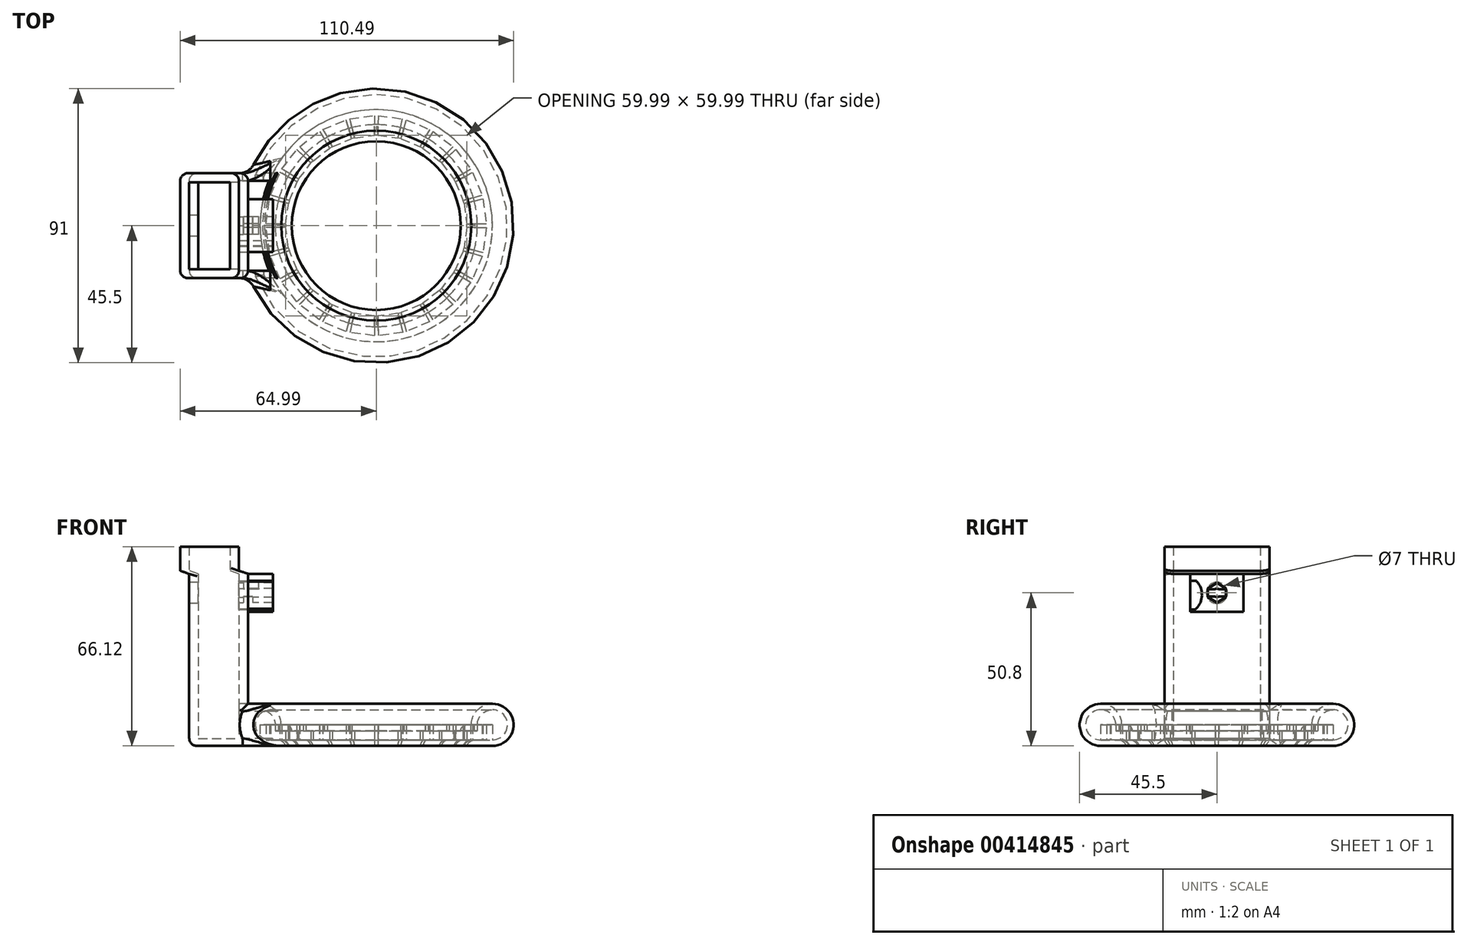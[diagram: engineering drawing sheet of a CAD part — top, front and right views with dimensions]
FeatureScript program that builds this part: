
annotation { "Feature Type Name" : "Feature", "Feature Type Description" : "" }
export const myFeature = defineFeature(function(context is Context, id is Id, definition is map)
    precondition{}
    {
        {
            var Q0;
            Q0=qCreatedBy(makeId("Right.planeOp"),FACE);
            cPlane(context, id + "F0", {"entities" : qUnion([Q0]), "cplaneType" : CPlaneType.OFFSET, "offset" : 42.5 * mm, "oppositeDirection" : true, "width" : 150 * mm, "height" : 150 * mm});
        }
        {
            var Q0;
            Q0=qCreatedBy(makeId("Front.planeOp"),FACE);
            cPlane(context, id + "F1", {"entities" : qUnion([Q0]), "cplaneType" : CPlaneType.OFFSET, "offset" : 17.41 * mm, "width" : 150 * mm, "height" : 150 * mm});
        }
        {
            var Q0;
            Q0=qCreatedBy(makeId("Front.planeOp"),FACE);
            cPlane(context, id + "F2", {"entities" : qUnion([Q0]), "cplaneType" : CPlaneType.OFFSET, "offset" : 17.41 * mm, "oppositeDirection" : true, "width" : 150 * mm, "height" : 150 * mm});
        }
        {
            var Q0;
            Q0=qCreatedBy(makeId("Top.planeOp"),FACE);
            cPlane(context, id + "F3", {"entities" : qUnion([Q0]), "cplaneType" : CPlaneType.OFFSET, "offset" : 7 * mm, "width" : 150 * mm, "height" : 150 * mm});
        }
        {
            var Q0;
            Q0=qCreatedBy(id+"F3.planeOp",FACE);
            cPlane(context, id + "F4", {"entities" : qUnion([Q0]), "cplaneType" : CPlaneType.OFFSET, "offset" : 6.95 * mm, "width" : 150 * mm, "height" : 150 * mm});
        }
        {
            var Q0;
            Q0=qCreatedBy(id+"F3.planeOp",FACE);
            cPlane(context, id + "F5", {"entities" : qUnion([Q0]), "cplaneType" : CPlaneType.OFFSET, "offset" : 50.12 * mm, "width" : 150 * mm, "height" : 150 * mm});
        }
        {
            var Q0;
            Q0=qCreatedBy(makeId("Right.planeOp"),FACE);
            cPlane(context, id + "F6", {"entities" : qUnion([Q0]), "cplaneType" : CPlaneType.OFFSET, "offset" : 62 * mm, "oppositeDirection" : true, "width" : 150 * mm, "height" : 150 * mm});
        }
        {
            var Q0;
            Q0=qCreatedBy(id+"F5.planeOp",FACE);
            cPlane(context, id + "F7", {"entities" : qUnion([Q0]), "cplaneType" : CPlaneType.OFFSET, "offset" : 1 * mm, "width" : 150 * mm, "height" : 150 * mm});
        }
        {
            var Q0;
            Q0=qCreatedBy(makeId("Top.planeOp"),FACE);
            var sketch = newSketch(context, id + "F8", { "sketchPlane" : qUnion([Q0])});
            skCircle(sketch, "E0", {"center": v(0, 0) * mm, "radius": 45 * mm});
            skCircle(sketch, "E1.0", {"center": v(0, 0) * mm, "radius": 38.5 * mm});
            skLineSegment(sketch, "E2", {"start": v(-136.41, 41.5) * mm, "end": v(-136.41, 35) * mm});
            skLineSegment(sketch, "E3", {"start": v(-128.72, 34) * mm, "end": v(-127.05, 40.28) * mm});
            skLineSegment(sketch, "E4", {"start": v(-118.16, 36.6) * mm, "end": v(-121.4, 30.99) * mm});
            skLineSegment(sketch, "E5", {"start": v(-115.15, 26.17) * mm, "end": v(-110.55, 30.76) * mm});
            skLineSegment(sketch, "E6", {"start": v(-110.44, 20.01) * mm, "end": v(-104.8, 23.26) * mm});
            skLineSegment(sketch, "E7", {"start": v(-107.45, 12.84) * mm, "end": v(-101.18, 14.54) * mm});
            skLineSegment(sketch, "E8", {"start": v(-106.41, 5.01) * mm, "end": v(-99.91, 5.01) * mm});
            skLineSegment(sketch, "E9.MirrorCS", {"start": v(-107.44, -2.81) * mm, "end": v(-101.17, -4.5) * mm});
            skLineSegment(sketch, "E10.MirrorCS", {"start": v(-110.42, -9.99) * mm, "end": v(-104.8, -13.24) * mm});
            skLineSegment(sketch, "E11.MirrorCS", {"start": v(-115.13, -16.15) * mm, "end": v(-110.52, -20.73) * mm});
            skLineSegment(sketch, "E12.MirrorCS", {"start": v(-118.13, -26.6) * mm, "end": v(-121.38, -20.97) * mm});
            skLineSegment(sketch, "E13.MirrorCS", {"start": v(-128.7, -24) * mm, "end": v(-127.02, -30.27) * mm});
            skLineSegment(sketch, "E14.MirrorCS", {"start": v(-144.1, 34) * mm, "end": v(-145.77, 40.28) * mm});
            skLineSegment(sketch, "E15.MirrorCS", {"start": v(-154.66, 36.6) * mm, "end": v(-151.41, 30.99) * mm});
            skLineSegment(sketch, "E16.MirrorCS", {"start": v(-157.67, 26.17) * mm, "end": v(-162.27, 30.76) * mm});
            skLineSegment(sketch, "E17.MirrorCS", {"start": v(-162.38, 20.01) * mm, "end": v(-168.01, 23.26) * mm});
            skLineSegment(sketch, "E18.MirrorCS", {"start": v(-165.37, 12.84) * mm, "end": v(-171.64, 14.54) * mm});
            skLineSegment(sketch, "E19.MirrorCS", {"start": v(-165.38, -2.81) * mm, "end": v(-171.65, -4.5) * mm});
            skLineSegment(sketch, "E20.MirrorCS", {"start": v(-162.4, -9.99) * mm, "end": v(-168.03, -13.24) * mm});
            skLineSegment(sketch, "E21.MirrorCS", {"start": v(-157.69, -16.15) * mm, "end": v(-162.3, -20.73) * mm});
            skLineSegment(sketch, "E22.MirrorCS", {"start": v(-154.69, -26.6) * mm, "end": v(-151.44, -20.97) * mm});
            skLineSegment(sketch, "E23.MirrorCS", {"start": v(-144.13, -24) * mm, "end": v(-145.8, -30.27) * mm});
            skLineSegment(sketch, "E24", {"start": v(-136.41, -25) * mm, "end": v(-136.41, -31.5) * mm});
            skLineSegment(sketch, "E25", {"start": v(-166.41, 5) * mm, "end": v(-172.91, 5) * mm});
            skCircle(sketch, "E26", {"center": v(-136.41, 5) * mm, "radius": 1.25 * mm, "construction": true});
            skLineSegment(sketch, "E27", {"start": v(0.64, 36.5) * mm, "end": v(0.52, 30) * mm});
            skLineSegment(sketch, "E28", {"start": v(8.2, 28.86) * mm, "end": v(9.97, 35.11) * mm});
            skLineSegment(sketch, "E29", {"start": v(18.8, 31.29) * mm, "end": v(15.46, 25.72) * mm});
            skLineSegment(sketch, "E30", {"start": v(21.62, 20.8) * mm, "end": v(26.3, 25.3) * mm});
            skLineSegment(sketch, "E31", {"start": v(26.23, 14.56) * mm, "end": v(31.92, 17.71) * mm});
            skLineSegment(sketch, "E32", {"start": v(29.1, 7.33) * mm, "end": v(35.4, 8.92) * mm});
            skLineSegment(sketch, "E33", {"start": v(30, -0.5) * mm, "end": v(36.5, -0.62) * mm});
            skLineSegment(sketch, "E34.MirrorCS", {"start": v(28.82, -8.32) * mm, "end": v(35.07, -10.12) * mm});
            skLineSegment(sketch, "E35.MirrorCS", {"start": v(25.72, -15.44) * mm, "end": v(31.3, -18.78) * mm});
            skLineSegment(sketch, "E36.MirrorCS", {"start": v(20.9, -21.52) * mm, "end": v(25.43, -26.18) * mm});
            skLineSegment(sketch, "E37.MirrorCS", {"start": v(17.73, -31.9) * mm, "end": v(14.57, -26.23) * mm});
            skLineSegment(sketch, "E38.MirrorCS", {"start": v(7.21, -29.12) * mm, "end": v(8.77, -35.43) * mm});
            skLineSegment(sketch, "E39.MirrorCS", {"start": v(-7.18, 29.13) * mm, "end": v(-8.74, 35.44) * mm});
            skLineSegment(sketch, "E40.MirrorCS", {"start": v(-17.7, 31.92) * mm, "end": v(-14.55, 26.25) * mm});
            skLineSegment(sketch, "E41.MirrorCS", {"start": v(-20.88, 21.54) * mm, "end": v(-25.4, 26.2) * mm});
            skLineSegment(sketch, "E42.MirrorCS", {"start": v(-25.7, 15.46) * mm, "end": v(-31.28, 18.81) * mm});
            skLineSegment(sketch, "E43.MirrorCS", {"start": v(-28.82, 8.34) * mm, "end": v(-35.06, 10.15) * mm});
            skLineSegment(sketch, "E44.MirrorCS", {"start": v(-29.1, -7.3) * mm, "end": v(-35.4, -8.89) * mm});
            skLineSegment(sketch, "E45.MirrorCS", {"start": v(-26.25, -14.53) * mm, "end": v(-31.93, -17.68) * mm});
            skLineSegment(sketch, "E46.MirrorCS", {"start": v(-21.64, -20.77) * mm, "end": v(-26.33, -25.28) * mm});
            skLineSegment(sketch, "E47.MirrorCS", {"start": v(-18.83, -31.27) * mm, "end": v(-15.48, -25.7) * mm});
            skLineSegment(sketch, "E48.MirrorCS", {"start": v(-8.22, -28.85) * mm, "end": v(-10, -35.1) * mm});
            skLineSegment(sketch, "E49", {"start": v(-0.52, -30) * mm, "end": v(-0.64, -36.5) * mm});
            skLineSegment(sketch, "E50", {"start": v(-30, 0.52) * mm, "end": v(-36.5, 0.64) * mm});
            skLineSegment(sketch, "E51", {"start": v(-0.64, 36.5) * mm, "end": v(-0.52, 30) * mm});
            skLineSegment(sketch, "E52", {"start": v(7.18, 29.13) * mm, "end": v(8.74, 35.44) * mm});
            skLineSegment(sketch, "E53", {"start": v(17.7, 31.92) * mm, "end": v(14.55, 26.25) * mm});
            skLineSegment(sketch, "E54", {"start": v(20.88, 21.54) * mm, "end": v(25.4, 26.2) * mm});
            skLineSegment(sketch, "E55", {"start": v(25.7, 15.46) * mm, "end": v(31.28, 18.81) * mm});
            skLineSegment(sketch, "E56", {"start": v(28.82, 8.34) * mm, "end": v(35.06, 10.15) * mm});
            skLineSegment(sketch, "E57", {"start": v(30, 0.54) * mm, "end": v(36.5, 0.65) * mm});
            skLineSegment(sketch, "E58.MirrorCS", {"start": v(29.1, -7.3) * mm, "end": v(35.4, -8.89) * mm});
            skLineSegment(sketch, "E59.MirrorCS", {"start": v(26.25, -14.53) * mm, "end": v(31.93, -17.68) * mm});
            skLineSegment(sketch, "E60.MirrorCS", {"start": v(21.64, -20.77) * mm, "end": v(26.33, -25.28) * mm});
            skLineSegment(sketch, "E61.MirrorCS", {"start": v(18.83, -31.27) * mm, "end": v(15.48, -25.7) * mm});
            skLineSegment(sketch, "E62.MirrorCS", {"start": v(8.22, -28.85) * mm, "end": v(10, -35.1) * mm});
            skLineSegment(sketch, "E63.MirrorCS", {"start": v(-8.2, 28.86) * mm, "end": v(-9.97, 35.11) * mm});
            skLineSegment(sketch, "E64.MirrorCS", {"start": v(-18.8, 31.29) * mm, "end": v(-15.46, 25.72) * mm});
            skLineSegment(sketch, "E65.MirrorCS", {"start": v(-21.62, 20.8) * mm, "end": v(-26.3, 25.3) * mm});
            skLineSegment(sketch, "E66.MirrorCS", {"start": v(-26.23, 14.56) * mm, "end": v(-31.92, 17.71) * mm});
            skLineSegment(sketch, "E67.MirrorCS", {"start": v(-29.1, 7.33) * mm, "end": v(-35.4, 8.92) * mm});
            skLineSegment(sketch, "E68.MirrorCS", {"start": v(-28.82, -8.32) * mm, "end": v(-35.07, -10.12) * mm});
            skLineSegment(sketch, "E69.MirrorCS", {"start": v(-25.72, -15.44) * mm, "end": v(-31.3, -18.78) * mm});
            skLineSegment(sketch, "E70.MirrorCS", {"start": v(-20.9, -21.52) * mm, "end": v(-25.43, -26.18) * mm});
            skLineSegment(sketch, "E71.MirrorCS", {"start": v(-17.73, -31.9) * mm, "end": v(-14.57, -26.23) * mm});
            skLineSegment(sketch, "E72.MirrorCS", {"start": v(-7.21, -29.12) * mm, "end": v(-8.77, -35.43) * mm});
            skLineSegment(sketch, "E73", {"start": v(0.52, -30) * mm, "end": v(0.64, -36.5) * mm});
            skLineSegment(sketch, "E74", {"start": v(-30, -0.52) * mm, "end": v(-36.5, -0.64) * mm});
            skCircle(sketch, "E75", {"center": v(0, 0) * mm, "radius": 1.25 * mm, "construction": true});
            skLineSegment(sketch, "E76", {"start": v(-29.1, 7.33) * mm, "end": v(-28.82, 8.34) * mm});
            skLineSegment(sketch, "E77", {"start": v(-28.82, 8.34) * mm, "end": v(-26.23, 14.56) * mm});
            skLineSegment(sketch, "E78", {"start": v(-26.23, 14.56) * mm, "end": v(-25.7, 15.46) * mm});
            skLineSegment(sketch, "E79", {"start": v(-25.7, 15.46) * mm, "end": v(-21.62, 20.8) * mm});
            skLineSegment(sketch, "E80", {"start": v(-21.62, 20.8) * mm, "end": v(-20.88, 21.54) * mm});
            skLineSegment(sketch, "E81", {"start": v(-20.88, 21.54) * mm, "end": v(-15.46, 25.72) * mm});
            skLineSegment(sketch, "E82", {"start": v(-15.46, 25.72) * mm, "end": v(-14.55, 26.25) * mm});
            skLineSegment(sketch, "E83", {"start": v(-14.55, 26.25) * mm, "end": v(-8.2, 28.86) * mm});
            skLineSegment(sketch, "E84", {"start": v(-8.2, 28.86) * mm, "end": v(-7.18, 29.13) * mm});
            skLineSegment(sketch, "E85", {"start": v(-7.18, 29.13) * mm, "end": v(-0.52, 30) * mm});
            skLineSegment(sketch, "E86", {"start": v(-0.52, 30) * mm, "end": v(0.52, 30) * mm});
            skLineSegment(sketch, "E87", {"start": v(0.52, 30) * mm, "end": v(7.18, 29.13) * mm});
            skLineSegment(sketch, "E88", {"start": v(7.18, 29.13) * mm, "end": v(8.2, 28.86) * mm});
            skLineSegment(sketch, "E89", {"start": v(8.2, 28.86) * mm, "end": v(14.55, 26.25) * mm});
            skLineSegment(sketch, "E90", {"start": v(14.55, 26.25) * mm, "end": v(15.46, 25.72) * mm});
            skLineSegment(sketch, "E91", {"start": v(15.46, 25.72) * mm, "end": v(20.88, 21.54) * mm});
            skLineSegment(sketch, "E92", {"start": v(20.88, 21.54) * mm, "end": v(21.62, 20.8) * mm});
            skLineSegment(sketch, "E93", {"start": v(21.62, 20.8) * mm, "end": v(25.7, 15.46) * mm});
            skLineSegment(sketch, "E94", {"start": v(25.7, 15.46) * mm, "end": v(26.23, 14.56) * mm});
            skLineSegment(sketch, "E95", {"start": v(26.23, 14.56) * mm, "end": v(28.82, 8.34) * mm});
            skLineSegment(sketch, "E96", {"start": v(28.82, 8.34) * mm, "end": v(29.1, 7.33) * mm});
            skLineSegment(sketch, "E97", {"start": v(29.1, 7.33) * mm, "end": v(30, 0.54) * mm});
            skLineSegment(sketch, "E98", {"start": v(30, 0.54) * mm, "end": v(30, -0.5) * mm});
            skLineSegment(sketch, "E99", {"start": v(30, -0.5) * mm, "end": v(29.1, -7.3) * mm});
            skLineSegment(sketch, "E100", {"start": v(29.1, -7.3) * mm, "end": v(28.82, -8.32) * mm});
            skLineSegment(sketch, "E101", {"start": v(28.82, -8.32) * mm, "end": v(26.25, -14.53) * mm});
            skLineSegment(sketch, "E102", {"start": v(26.25, -14.53) * mm, "end": v(25.72, -15.44) * mm});
            skLineSegment(sketch, "E103", {"start": v(25.72, -15.44) * mm, "end": v(21.64, -20.77) * mm});
            skLineSegment(sketch, "E104", {"start": v(21.64, -20.77) * mm, "end": v(20.9, -21.52) * mm});
            skLineSegment(sketch, "E105", {"start": v(20.9, -21.52) * mm, "end": v(15.48, -25.7) * mm});
            skLineSegment(sketch, "E106", {"start": v(15.48, -25.7) * mm, "end": v(14.57, -26.23) * mm});
            skLineSegment(sketch, "E107", {"start": v(14.57, -26.23) * mm, "end": v(8.22, -28.85) * mm});
            skLineSegment(sketch, "E108", {"start": v(8.22, -28.85) * mm, "end": v(7.21, -29.12) * mm});
            skLineSegment(sketch, "E109", {"start": v(7.21, -29.12) * mm, "end": v(0.52, -30) * mm});
            skLineSegment(sketch, "E110", {"start": v(0.52, -30) * mm, "end": v(-0.52, -30) * mm});
            skLineSegment(sketch, "E111", {"start": v(-0.52, -30) * mm, "end": v(-7.21, -29.12) * mm});
            skLineSegment(sketch, "E112", {"start": v(-7.21, -29.12) * mm, "end": v(-8.22, -28.85) * mm});
            skLineSegment(sketch, "E113", {"start": v(-8.22, -28.85) * mm, "end": v(-14.57, -26.23) * mm});
            skLineSegment(sketch, "E114", {"start": v(-14.57, -26.23) * mm, "end": v(-15.48, -25.7) * mm});
            skLineSegment(sketch, "E115", {"start": v(-15.48, -25.7) * mm, "end": v(-20.9, -21.52) * mm});
            skLineSegment(sketch, "E116", {"start": v(-20.9, -21.52) * mm, "end": v(-21.64, -20.77) * mm});
            skLineSegment(sketch, "E117", {"start": v(-21.64, -20.77) * mm, "end": v(-25.72, -15.44) * mm});
            skLineSegment(sketch, "E118", {"start": v(-25.72, -15.44) * mm, "end": v(-26.25, -14.53) * mm});
            skLineSegment(sketch, "E119", {"start": v(-28.82, -8.32) * mm, "end": v(-29.1, -7.3) * mm});
            skLineSegment(sketch, "E120", {"start": v(-26.25, -14.53) * mm, "end": v(-28.82, -8.32) * mm});
            skLineSegment(sketch, "E121", {"start": v(-29.1, -7.3) * mm, "end": v(-30, -0.52) * mm});
            skLineSegment(sketch, "E122", {"start": v(-30, -0.52) * mm, "end": v(-30, 0.52) * mm});
            skLineSegment(sketch, "E123", {"start": v(-30, 0.52) * mm, "end": v(-29.1, 7.33) * mm});
            skLineSegment(sketch, "E124", {"start": v(-36.5, 0.64) * mm, "end": v(-35.4, 8.92) * mm});
            skLineSegment(sketch, "E125", {"start": v(-35.06, 10.15) * mm, "end": v(-31.92, 17.71) * mm});
            skLineSegment(sketch, "E126", {"start": v(-31.28, 18.81) * mm, "end": v(-26.3, 25.3) * mm});
            skLineSegment(sketch, "E127", {"start": v(-25.4, 26.2) * mm, "end": v(-18.8, 31.29) * mm});
            skLineSegment(sketch, "E128", {"start": v(-17.7, 31.92) * mm, "end": v(-9.97, 35.11) * mm});
            skLineSegment(sketch, "E129", {"start": v(-8.74, 35.44) * mm, "end": v(-0.64, 36.5) * mm});
            skLineSegment(sketch, "E130", {"start": v(0.64, 36.5) * mm, "end": v(8.74, 35.44) * mm});
            skLineSegment(sketch, "E131", {"start": v(9.97, 35.11) * mm, "end": v(17.7, 31.92) * mm});
            skLineSegment(sketch, "E132", {"start": v(18.8, 31.29) * mm, "end": v(25.4, 26.2) * mm});
            skLineSegment(sketch, "E133", {"start": v(26.3, 25.3) * mm, "end": v(31.28, 18.81) * mm});
            skLineSegment(sketch, "E134", {"start": v(31.92, 17.71) * mm, "end": v(35.06, 10.15) * mm});
            skLineSegment(sketch, "E135", {"start": v(35.4, 8.92) * mm, "end": v(36.5, 0.65) * mm});
            skLineSegment(sketch, "E136", {"start": v(36.5, -0.62) * mm, "end": v(35.4, -8.89) * mm});
            skLineSegment(sketch, "E137", {"start": v(35.07, -10.12) * mm, "end": v(31.93, -17.68) * mm});
            skLineSegment(sketch, "E138", {"start": v(31.3, -18.78) * mm, "end": v(26.33, -25.28) * mm});
            skLineSegment(sketch, "E139", {"start": v(25.43, -26.18) * mm, "end": v(18.83, -31.27) * mm});
            skLineSegment(sketch, "E140", {"start": v(17.73, -31.9) * mm, "end": v(10, -35.1) * mm});
            skLineSegment(sketch, "E141", {"start": v(8.77, -35.43) * mm, "end": v(0.64, -36.5) * mm});
            skLineSegment(sketch, "E142", {"start": v(-0.64, -36.5) * mm, "end": v(-8.77, -35.43) * mm});
            skLineSegment(sketch, "E143", {"start": v(-10, -35.1) * mm, "end": v(-17.73, -31.9) * mm});
            skLineSegment(sketch, "E144", {"start": v(-18.83, -31.27) * mm, "end": v(-25.43, -26.18) * mm});
            skLineSegment(sketch, "E145", {"start": v(-26.33, -25.28) * mm, "end": v(-31.3, -18.78) * mm});
            skLineSegment(sketch, "E146", {"start": v(-31.93, -17.68) * mm, "end": v(-35.07, -10.12) * mm});
            skLineSegment(sketch, "E147", {"start": v(-35.4, -8.89) * mm, "end": v(-36.5, -0.64) * mm});
            skSolve(sketch);
        }
        {
            var Q0;
            Q0=qCreatedBy(makeId("Front.planeOp"),FACE);
            var sketch = newSketch(context, id + "F9", { "sketchPlane" : qUnion([Q0])});
            skLineSegment(sketch, "E148.bottom", {"start": v(38.5, 7) * mm, "end": v(-38.5, 7) * mm, "construction": true});
            skLineSegment(sketch, "E148.top", {"start": v(38.5, -7) * mm, "end": v(-38.5, -7) * mm, "construction": true});
            skLineSegment(sketch, "E148.left", {"start": v(38.5, 7) * mm, "end": v(38.5, -7) * mm, "construction": true});
            skLineSegment(sketch, "E148.right", {"start": v(-38.5, 7) * mm, "end": v(-38.5, -7) * mm, "construction": true});
            skPoint(sketch, "E148.middle", {"position": v(0, 0) * mm});
            skLineSegment(sketch, "E149", {"start": v(-38.5, 0) * mm, "end": v(38.5, 0) * mm, "construction": true});
            skArc(sketch, "E150", {"start": v(38.5, 0) * mm, "mid": v(43.45, 11.95) * mm, "end": v(31.5, 7) * mm});
            skArc(sketch, "E151", {"start": v(38.5, 2) * mm, "mid": v(42.04, 10.54) * mm, "end": v(33.5, 7) * mm});
            skLineSegment(sketch, "E152", {"start": v(38.5, 2) * mm, "end": v(38.5, 0) * mm});
            skLineSegment(sketch, "E153", {"start": v(38.5, 2) * mm, "end": v(31.5, 2) * mm, "construction": true});
            skLineSegment(sketch, "E154", {"start": v(31.5, 2) * mm, "end": v(31.5, 0) * mm, "construction": true});
            skLineSegment(sketch, "E155.0", {"start": v(38.5, 5) * mm, "end": v(-38.5, 5) * mm, "construction": true});
            skLineSegment(sketch, "E156", {"start": v(30, 0) * mm, "end": v(30, 7) * mm, "construction": true});
            skLineSegment(sketch, "E157", {"start": v(31.5, 7) * mm, "end": v(30, 7) * mm});
            skLineSegment(sketch, "E158", {"start": v(30, 7) * mm, "end": v(30, 5) * mm});
            skLineSegment(sketch, "E159", {"start": v(30, 5) * mm, "end": v(33.5, 5) * mm});
            skLineSegment(sketch, "E160", {"start": v(33.5, 5) * mm, "end": v(33.5, 7) * mm});
            skLineSegment(sketch, "E161", {"start": v(0, -7) * mm, "end": v(0, 7) * mm, "construction": true});
            skLineSegment(sketch, "E162", {"start": v(38.5, 7) * mm, "end": v(38.5, 14) * mm, "construction": true});
            skLineSegment(sketch, "E163", {"start": v(38.5, 7) * mm, "end": v(45.5, 7) * mm, "construction": true});
            skLineSegment(sketch, "E164", {"start": v(38.5, 12) * mm, "end": v(38.5, 14) * mm});
            skLineSegment(sketch, "E165", {"start": v(43.5, 7) * mm, "end": v(45.5, 7) * mm});
            skLineSegment(sketch, "E166.MirrorCS", {"start": v(-38.5, 2) * mm, "end": v(-38.5, 0) * mm});
            skLineSegment(sketch, "E167.MirrorCS", {"start": v(-30, 7) * mm, "end": v(-30, 5) * mm});
            skLineSegment(sketch, "E168.MirrorCS", {"start": v(-31.5, 7) * mm, "end": v(-30, 7) * mm});
            skLineSegment(sketch, "E169.MirrorCS", {"start": v(-33.5, 5) * mm, "end": v(-33.5, 7) * mm});
            skLineSegment(sketch, "E170.MirrorCS", {"start": v(-43.5, 7) * mm, "end": v(-45.5, 7) * mm});
            skLineSegment(sketch, "E171.MirrorCS", {"start": v(-30, 5) * mm, "end": v(-33.5, 5) * mm});
            skLineSegment(sketch, "E172.MirrorCS", {"start": v(-31.5, 2) * mm, "end": v(-31.5, 0) * mm, "construction": true});
            skLineSegment(sketch, "E173.MirrorCS", {"start": v(-38.5, 12) * mm, "end": v(-38.5, 14) * mm});
            skLineSegment(sketch, "E174.MirrorCS", {"start": v(-38.5, 7) * mm, "end": v(-45.5, 7) * mm, "construction": true});
            skLineSegment(sketch, "E175.MirrorCS", {"start": v(-38.5, 2) * mm, "end": v(-31.5, 2) * mm, "construction": true});
            skLineSegment(sketch, "E176.MirrorCS", {"start": v(-38.5, 7) * mm, "end": v(-38.5, 14) * mm, "construction": true});
            skArc(sketch, "E177.MirrorCS", {"start": v(-38.5, 0) * mm, "mid": v(-43.45, 11.95) * mm, "end": v(-31.5, 7) * mm});
            skArc(sketch, "E178.MirrorCS", {"start": v(-38.5, 2) * mm, "mid": v(-42.04, 10.54) * mm, "end": v(-33.5, 7) * mm});
            skLineSegment(sketch, "E179.MirrorCS", {"start": v(-38.5, 5) * mm, "end": v(38.5, 5) * mm, "construction": true});
            skLineSegment(sketch, "E180.MirrorCS", {"start": v(-30, 0) * mm, "end": v(-30, 7) * mm, "construction": true});
            skLineSegment(sketch, "E181.MirrorCS", {"start": v(-38.5, 7) * mm, "end": v(38.5, 7) * mm, "construction": true});
            skArc(sketch, "E182", {"start": v(30, 7) * mm, "mid": v(28.58, 6.41) * mm, "end": v(28, 5) * mm});
            skLineSegment(sketch, "E183", {"start": v(28, 5) * mm, "end": v(30, 5) * mm});
            skArc(sketch, "E184.MirrorCS", {"start": v(-30, 7) * mm, "mid": v(-28.58, 6.41) * mm, "end": v(-28, 5) * mm});
            skLineSegment(sketch, "E185", {"start": v(-30, 5) * mm, "end": v(-28, 5) * mm});
            skSolve(sketch);
        }
        {
            var Q0;
            Q0=qCreatedBy(id+"F0.planeOp",FACE);
            var sketch = newSketch(context, id + "F10", { "sketchPlane" : qUnion([Q0])});
            skLineSegment(sketch, "E186.bottom", {"start": v(45.5, 14) * mm, "end": v(-45.5, 14) * mm, "construction": true});
            skLineSegment(sketch, "E186.top", {"start": v(45.5, -14) * mm, "end": v(-45.5, -14) * mm, "construction": true});
            skLineSegment(sketch, "E186.left", {"start": v(45.5, 14) * mm, "end": v(45.5, -14) * mm, "construction": true});
            skLineSegment(sketch, "E186.right", {"start": v(-45.5, 14) * mm, "end": v(-45.5, -14) * mm, "construction": true});
            skPoint(sketch, "E186.middle", {"position": v(0, 0) * mm});
            skLineSegment(sketch, "E187", {"start": v(-45.5, 0) * mm, "end": v(45.5, 0) * mm, "construction": true});
            skLineSegment(sketch, "E188", {"start": v(0, 14) * mm, "end": v(0, -14) * mm, "construction": true});
            skLineSegment(sketch, "E189.0", {"start": v(-17.41, 14) * mm, "end": v(-17.41, -14) * mm, "construction": true});
            skLineSegment(sketch, "E190.MirrorCS", {"start": v(17.41, 14) * mm, "end": v(17.41, -14) * mm, "construction": true});
            skLineSegment(sketch, "E191.0", {"start": v(45.5, 7) * mm, "end": v(-45.5, 7) * mm, "construction": true});
            skLineSegment(sketch, "E192", {"start": v(-17.41, 14) * mm, "end": v(-17.41, 7) * mm});
            skLineSegment(sketch, "E193", {"start": v(-17.41, 7) * mm, "end": v(17.41, 7) * mm});
            skLineSegment(sketch, "E194", {"start": v(17.41, 7) * mm, "end": v(17.41, 14) * mm});
            skLineSegment(sketch, "E195", {"start": v(17.41, 14) * mm, "end": v(-17.41, 14) * mm});
            skLineSegment(sketch, "E196.0", {"start": v(45.5, 12) * mm, "end": v(-45.5, 12) * mm, "construction": true});
            skLineSegment(sketch, "E197.0", {"start": v(-14.73, 14) * mm, "end": v(-14.73, -14) * mm, "construction": true});
            skLineSegment(sketch, "E198.MirrorCS", {"start": v(14.73, 14) * mm, "end": v(14.73, -14) * mm, "construction": true});
            skLineSegment(sketch, "E199", {"start": v(-14.73, 7) * mm, "end": v(-14.73, 14) * mm});
            skLineSegment(sketch, "E200", {"start": v(14.73, 7) * mm, "end": v(14.73, 14) * mm});
            skLineSegment(sketch, "E201", {"start": v(17.41, 12) * mm, "end": v(-17.41, 12) * mm});
            skPoint(sketch, "E201.startSnap0", {"position": v(17.41, 10.5) * mm});
            skArc(sketch, "E202.0", {"start": v(6.63, 54.56) * mm, "mid": v(4.95, 49.97) * mm, "end": v(6.87, 45.48) * mm});
            skArc(sketch, "E203.MirrorCS", {"start": v(-6.63, 54.56) * mm, "mid": v(-4.95, 49.97) * mm, "end": v(-6.87, 45.48) * mm});
            skLineSegment(sketch, "E204", {"start": v(-6.63, 54.73) * mm, "end": v(6.63, 54.73) * mm});
            skLineSegment(sketch, "E205.1", {"start": v(-2.98, 46.95) * mm, "end": v(2.98, 46.95) * mm});
            skLineSegment(sketch, "E206", {"start": v(-8.8, 44.55) * mm, "end": v(-8.8, 57.13) * mm});
            skLineSegment(sketch, "E207.MirrorCS", {"start": v(8.8, 44.55) * mm, "end": v(8.8, 57.13) * mm});
            skLineSegment(sketch, "E208", {"start": v(-8.8, 57.13) * mm, "end": v(8.8, 57.13) * mm});
            skLineSegment(sketch, "E209", {"start": v(-6.63, 54.73) * mm, "end": v(-8.8, 54.73) * mm});
            skLineSegment(sketch, "E210", {"start": v(6.63, 54.73) * mm, "end": v(8.8, 54.73) * mm});
            skLineSegment(sketch, "E211", {"start": v(-2.98, 46.95) * mm, "end": v(-6.87, 45.27) * mm});
            skLineSegment(sketch, "E212", {"start": v(-6.87, 45.48) * mm, "end": v(-6.87, 45.27) * mm});
            skLineSegment(sketch, "E213.MirrorCS", {"start": v(2.98, 46.95) * mm, "end": v(6.87, 45.27) * mm});
            skLineSegment(sketch, "E214.MirrorCS", {"start": v(6.87, 45.48) * mm, "end": v(6.87, 45.27) * mm});
            skLineSegment(sketch, "E215", {"start": v(-8.8, 44.55) * mm, "end": v(8.8, 44.55) * mm});
            skLineSegment(sketch, "E216", {"start": v(6.87, 45.27) * mm, "end": v(8.8, 45.27) * mm});
            skLineSegment(sketch, "E217", {"start": v(-6.87, 45.27) * mm, "end": v(-8.8, 45.27) * mm});
            skCircle(sketch, "E218", {"center": v(0, 0) * mm, "radius": 1.5 * mm, "construction": true});
            skCircle(sketch, "E219", {"center": v(0, 50.8) * mm, "radius": 1.39 * mm});
            skLineSegment(sketch, "E220", {"start": v(6.63, 54.56) * mm, "end": v(6.63, 54.73) * mm});
            skLineSegment(sketch, "E221", {"start": v(-6.63, 54.56) * mm, "end": v(-6.63, 54.73) * mm});
            skLineSegment(sketch, "E222.1", {"start": v(0, 47.5) * mm, "end": v(2.95, 49.36) * mm});
            skLineSegment(sketch, "E222.2", {"start": v(-2.95, 49.36) * mm, "end": v(0, 47.5) * mm});
            skLineSegment(sketch, "E223.MirrorCS", {"start": v(0, 54.1) * mm, "end": v(2.95, 52.25) * mm});
            skLineSegment(sketch, "E224.MirrorCS", {"start": v(-2.95, 52.25) * mm, "end": v(0, 54.1) * mm});
            skLineSegment(sketch, "E225", {"start": v(2.95, 52.25) * mm, "end": v(2.95, 49.36) * mm});
            skLineSegment(sketch, "E226", {"start": v(-2.95, 52.25) * mm, "end": v(-2.95, 49.36) * mm});
            skCircle(sketch, "E227", {"center": v(0, 50.8) * mm, "radius": 1.25 * mm, "construction": true});
            skLineSegment(sketch, "E228", {"start": v(-2.95, 49.55) * mm, "end": v(2.95, 49.55) * mm});
            skLineSegment(sketch, "E229", {"start": v(-2.95, 52.05) * mm, "end": v(2.95, 52.05) * mm});
            skLineSegment(sketch, "E230", {"start": v(14.73, 14) * mm, "end": v(14.73, 52.5) * mm});
            skLineSegment(sketch, "E231", {"start": v(0, 55.8) * mm, "end": v(0, 14) * mm, "construction": true});
            skLineSegment(sketch, "E232.MirrorCS", {"start": v(-14.73, 14) * mm, "end": v(-14.73, 52.5) * mm});
            skLineSegment(sketch, "E233", {"start": v(17.41, 14) * mm, "end": v(17.41, 52.5) * mm});
            skLineSegment(sketch, "E234", {"start": v(-17.41, 14) * mm, "end": v(-17.41, 52.5) * mm});
            skLineSegment(sketch, "E235", {"start": v(-8.8, 57.13) * mm, "end": v(-17.41, 57.13) * mm});
            skLineSegment(sketch, "E236", {"start": v(8.8, 57.13) * mm, "end": v(17.41, 57.13) * mm});
            skLineSegment(sketch, "E237", {"start": v(17.41, 47.5) * mm, "end": v(17.41, 57.13) * mm});
            skLineSegment(sketch, "E238", {"start": v(14.73, 47.5) * mm, "end": v(14.73, 57.13) * mm});
            skLineSegment(sketch, "E239", {"start": v(-14.73, 47.5) * mm, "end": v(-14.73, 57.13) * mm});
            skLineSegment(sketch, "E240", {"start": v(-17.41, 47.5) * mm, "end": v(-17.41, 57.13) * mm});
            skSolve(sketch);
        }
        {
            var Q0;
            Q0=qCreatedBy(id+"F1.planeOp",FACE);
            var sketch = newSketch(context, id + "F11", { "sketchPlane" : qUnion([Q0])});
            skLineSegment(sketch, "E241.bottom", {"start": v(45.5, 14) * mm, "end": v(-45.5, 14) * mm, "construction": true});
            skLineSegment(sketch, "E241.top", {"start": v(45.5, -14) * mm, "end": v(-45.5, -14) * mm, "construction": true});
            skLineSegment(sketch, "E241.left", {"start": v(45.5, 14) * mm, "end": v(45.5, -14) * mm, "construction": true});
            skLineSegment(sketch, "E241.right", {"start": v(-45.5, 14) * mm, "end": v(-45.5, -14) * mm, "construction": true});
            skPoint(sketch, "E241.middle", {"position": v(0, 0) * mm});
            skLineSegment(sketch, "E242", {"start": v(-45.5, 0) * mm, "end": v(45.5, 0) * mm, "construction": true});
            skLineSegment(sketch, "E243", {"start": v(0, 14) * mm, "end": v(0, -14) * mm, "construction": true});
            skLineSegment(sketch, "E244.0", {"start": v(-17.41, 14) * mm, "end": v(-17.41, -14) * mm, "construction": true});
            skLineSegment(sketch, "E245.MirrorCS", {"start": v(17.41, 14) * mm, "end": v(17.41, -14) * mm, "construction": true});
            skLineSegment(sketch, "E246.0", {"start": v(45.5, 7) * mm, "end": v(-45.5, 7) * mm, "construction": true});
            skLineSegment(sketch, "E247", {"start": v(-17.41, 14) * mm, "end": v(-17.41, 7) * mm});
            skLineSegment(sketch, "E248", {"start": v(-17.41, 7) * mm, "end": v(17.41, 7) * mm});
            skLineSegment(sketch, "E249", {"start": v(17.41, 7) * mm, "end": v(17.41, 14) * mm});
            skLineSegment(sketch, "E250", {"start": v(17.41, 14) * mm, "end": v(-17.41, 14) * mm});
            skLineSegment(sketch, "E251.0", {"start": v(45.5, 12) * mm, "end": v(-45.5, 12) * mm, "construction": true});
            skLineSegment(sketch, "E252.0", {"start": v(-14.73, 14) * mm, "end": v(-14.73, -14) * mm, "construction": true});
            skLineSegment(sketch, "E253.MirrorCS", {"start": v(14.73, 14) * mm, "end": v(14.73, -14) * mm, "construction": true});
            skLineSegment(sketch, "E254", {"start": v(-14.73, 7) * mm, "end": v(-14.73, 14) * mm});
            skLineSegment(sketch, "E255", {"start": v(14.73, 7) * mm, "end": v(14.73, 14) * mm});
            skLineSegment(sketch, "E256", {"start": v(17.41, 12) * mm, "end": v(-17.41, 12) * mm});
            skPoint(sketch, "E256.startSnap0", {"position": v(17.41, 10.5) * mm});
            skLineSegment(sketch, "E257", {"start": v(45.5, 14) * mm, "end": v(45.5, 7) * mm});
            skCircle(sketch, "E258", {"center": v(-35.07, 7) * mm, "radius": 7 * mm, "construction": true});
            skArc(sketch, "E259", {"start": v(-35.07, 12) * mm, "mid": v(-40.07, 7) * mm, "end": v(-35.07, 2) * mm});
            skLineSegment(sketch, "E260", {"start": v(-35.07, 12) * mm, "end": v(-35.07, 14) * mm});
            skLineSegment(sketch, "E261", {"start": v(-35.07, 14) * mm, "end": v(-45.5, 14) * mm});
            skLineSegment(sketch, "E262", {"start": v(-45.5, 14) * mm, "end": v(-45.5, 0) * mm});
            skLineSegment(sketch, "E263", {"start": v(-45.5, 0) * mm, "end": v(-35.07, 0) * mm});
            skLineSegment(sketch, "E264", {"start": v(-35.07, 0) * mm, "end": v(-35.07, 2) * mm});
            skLineSegment(sketch, "E265.MirrorCS", {"start": v(45.5, 2) * mm, "end": v(-45.5, 2) * mm, "construction": true});
            skCircle(sketch, "E266", {"center": v(0, 7) * mm, "radius": 1.25 * mm, "construction": true});
            skSolve(sketch);
        }
        {
            var Q0;
            Q0=qCreatedBy(id+"F2.planeOp",FACE);
            var sketch = newSketch(context, id + "F12", { "sketchPlane" : qUnion([Q0])});
            skLineSegment(sketch, "E267.bottom", {"start": v(45.5, 14) * mm, "end": v(-45.5, 14) * mm, "construction": true});
            skLineSegment(sketch, "E267.top", {"start": v(45.5, -14) * mm, "end": v(-45.5, -14) * mm, "construction": true});
            skLineSegment(sketch, "E267.left", {"start": v(45.5, 14) * mm, "end": v(45.5, -14) * mm, "construction": true});
            skLineSegment(sketch, "E267.right", {"start": v(-45.5, 14) * mm, "end": v(-45.5, -14) * mm, "construction": true});
            skPoint(sketch, "E267.middle", {"position": v(0, 0) * mm});
            skLineSegment(sketch, "E268", {"start": v(-45.5, 0) * mm, "end": v(45.5, 0) * mm, "construction": true});
            skLineSegment(sketch, "E269", {"start": v(0, 14) * mm, "end": v(0, -14) * mm, "construction": true});
            skLineSegment(sketch, "E270.0", {"start": v(-17.41, 14) * mm, "end": v(-17.41, -14) * mm, "construction": true});
            skLineSegment(sketch, "E271.MirrorCS", {"start": v(17.41, 14) * mm, "end": v(17.41, -14) * mm, "construction": true});
            skLineSegment(sketch, "E272.0", {"start": v(45.5, 7) * mm, "end": v(-45.5, 7) * mm, "construction": true});
            skLineSegment(sketch, "E273", {"start": v(-17.41, 14) * mm, "end": v(-17.41, 7) * mm});
            skLineSegment(sketch, "E274", {"start": v(-17.41, 7) * mm, "end": v(17.41, 7) * mm});
            skLineSegment(sketch, "E275", {"start": v(17.41, 7) * mm, "end": v(17.41, 14) * mm});
            skLineSegment(sketch, "E276", {"start": v(17.41, 14) * mm, "end": v(-17.41, 14) * mm});
            skLineSegment(sketch, "E277.0", {"start": v(45.5, 12) * mm, "end": v(-45.5, 12) * mm, "construction": true});
            skLineSegment(sketch, "E278.0", {"start": v(-14.73, 14) * mm, "end": v(-14.73, -14) * mm, "construction": true});
            skLineSegment(sketch, "E279.MirrorCS", {"start": v(14.73, 14) * mm, "end": v(14.73, -14) * mm, "construction": true});
            skLineSegment(sketch, "E280", {"start": v(-14.73, 7) * mm, "end": v(-14.73, 14) * mm});
            skLineSegment(sketch, "E281", {"start": v(14.73, 7) * mm, "end": v(14.73, 14) * mm});
            skLineSegment(sketch, "E282", {"start": v(17.41, 12) * mm, "end": v(-17.41, 12) * mm});
            skPoint(sketch, "E282.startSnap0", {"position": v(17.41, 10.5) * mm});
            skLineSegment(sketch, "E283", {"start": v(45.5, 14) * mm, "end": v(45.5, 7) * mm});
            skCircle(sketch, "E284", {"center": v(-35.07, 7) * mm, "radius": 7 * mm, "construction": true});
            skArc(sketch, "E285", {"start": v(-35.07, 12) * mm, "mid": v(-40.07, 7) * mm, "end": v(-35.07, 2) * mm});
            skLineSegment(sketch, "E286", {"start": v(-35.07, 12) * mm, "end": v(-35.07, 14) * mm});
            skLineSegment(sketch, "E287", {"start": v(-35.07, 14) * mm, "end": v(-45.5, 14) * mm});
            skLineSegment(sketch, "E288", {"start": v(-45.5, 14) * mm, "end": v(-45.5, 0) * mm});
            skLineSegment(sketch, "E289", {"start": v(-45.5, 0) * mm, "end": v(-35.07, 0) * mm});
            skLineSegment(sketch, "E290", {"start": v(-35.07, 0) * mm, "end": v(-35.07, 2) * mm});
            skLineSegment(sketch, "E291.MirrorCS", {"start": v(45.5, 2) * mm, "end": v(-45.5, 2) * mm, "construction": true});
            skCircle(sketch, "E292", {"center": v(0, 7) * mm, "radius": 1.25 * mm, "construction": true});
            skSolve(sketch);
        }
        {
            var Q0;
            Q0=qCreatedBy(makeId("Top.planeOp"),FACE);
            var sketch = newSketch(context, id + "F13", { "sketchPlane" : qUnion([Q0])});
            skPoint(sketch, "E293.middle", {"position": v(0, 0) * mm});
            skCircle(sketch, "E294", {"center": v(0, 0) * mm, "radius": 2.5 * mm, "construction": true});
            skLineSegment(sketch, "E295.MirrorCS", {"start": v(-32.65, 17.41) * mm, "end": v(-45.5, 17.41) * mm});
            skLineSegment(sketch, "E296.MirrorCS", {"start": v(-32.65, -17.41) * mm, "end": v(-45.5, -17.41) * mm});
            skLineSegment(sketch, "E297.MirrorCS", {"start": v(-45.5, 17.41) * mm, "end": v(-45.5, -17.41) * mm});
            skArc(sketch, "E298", {"start": v(-32.65, 17.41) * mm, "mid": v(-37, 0) * mm, "end": v(-32.65, -17.41) * mm});
            skLineSegment(sketch, "E299.bottom", {"start": v(-45.5, 8.28) * mm, "end": v(-45.5, -8.52) * mm, "construction": true});
            skLineSegment(sketch, "E299.left", {"start": v(-45.5, 8.28) * mm, "end": v(-59, 8.28) * mm, "construction": true});
            skLineSegment(sketch, "E300", {"start": v(-45.5, -8.52) * mm, "end": v(-59, -8.52) * mm, "construction": true});
            skLineSegment(sketch, "E301", {"start": v(-59, -8.52) * mm, "end": v(-59, 8.28) * mm, "construction": true});
            skLineSegment(sketch, "E302", {"start": v(-45.5, 8.28) * mm, "end": v(-59, -8.52) * mm, "construction": true});
            skLineSegment(sketch, "E303", {"start": v(-45.5, -8.52) * mm, "end": v(-59, 8.28) * mm, "construction": true});
            skLineSegment(sketch, "E304", {"start": v(-52.24, 0) * mm, "end": v(-42.5, 0) * mm, "construction": true});
            skLineSegment(sketch, "E305", {"start": v(-27.2, 0) * mm, "end": v(-42.4, 0) * mm, "construction": true});
            skLineSegment(sketch, "E306.0", {"start": v(-62, -8.52) * mm, "end": v(-62, 8.28) * mm, "construction": true});
            skLineSegment(sketch, "E307", {"start": v(-45.5, 17.41) * mm, "end": v(-62, 17.41) * mm});
            skLineSegment(sketch, "E308", {"start": v(-62, 17.41) * mm, "end": v(-62, -17.41) * mm});
            skLineSegment(sketch, "E309", {"start": v(-62, -17.41) * mm, "end": v(-45.5, -17.41) * mm});
            skLineSegment(sketch, "E310.0", {"start": v(-59, -14.41) * mm, "end": v(-45.5, -14.41) * mm});
            skLineSegment(sketch, "E310.1", {"start": v(-59, 14.41) * mm, "end": v(-59, -14.41) * mm});
            skLineSegment(sketch, "E310.2", {"start": v(-45.5, 14.41) * mm, "end": v(-59, 14.41) * mm});
            skSolve(sketch);
        }
        {
            var Q0;
            Q0=qCreatedBy(id+"F4.planeOp",FACE);
            var sketch = newSketch(context, id + "F14", { "sketchPlane" : qUnion([Q0])});
            skPoint(sketch, "E311.middle", {"position": v(0, 0) * mm});
            skCircle(sketch, "E312", {"center": v(0, 0) * mm, "radius": 2.5 * mm, "construction": true});
            skLineSegment(sketch, "E313.MirrorCS", {"start": v(-32.65, 17.41) * mm, "end": v(-45.5, 17.41) * mm});
            skLineSegment(sketch, "E314.MirrorCS", {"start": v(-32.65, -17.41) * mm, "end": v(-45.5, -17.41) * mm});
            skLineSegment(sketch, "E315.MirrorCS", {"start": v(-45.5, 17.41) * mm, "end": v(-45.5, -17.41) * mm});
            skArc(sketch, "E316", {"start": v(-32.65, 17.41) * mm, "mid": v(-37, 0) * mm, "end": v(-32.65, -17.41) * mm});
            skLineSegment(sketch, "E317.bottom", {"start": v(-45.5, 8.28) * mm, "end": v(-45.5, -8.52) * mm, "construction": true});
            skLineSegment(sketch, "E317.left", {"start": v(-45.5, 8.28) * mm, "end": v(-59, 8.28) * mm, "construction": true});
            skLineSegment(sketch, "E318", {"start": v(-45.5, -8.52) * mm, "end": v(-59, -8.52) * mm, "construction": true});
            skLineSegment(sketch, "E319", {"start": v(-59, -8.52) * mm, "end": v(-59, 8.28) * mm, "construction": true});
            skLineSegment(sketch, "E320", {"start": v(-45.5, 8.28) * mm, "end": v(-59, -8.52) * mm, "construction": true});
            skLineSegment(sketch, "E321", {"start": v(-45.5, -8.52) * mm, "end": v(-59, 8.28) * mm, "construction": true});
            skLineSegment(sketch, "E322", {"start": v(-52.24, 0) * mm, "end": v(-42.5, 0) * mm, "construction": true});
            skLineSegment(sketch, "E323", {"start": v(-27.2, 0) * mm, "end": v(-42.4, 0) * mm, "construction": true});
            skLineSegment(sketch, "E324.0", {"start": v(-62, -8.52) * mm, "end": v(-62, 8.28) * mm, "construction": true});
            skLineSegment(sketch, "E325", {"start": v(-45.5, 17.41) * mm, "end": v(-62, 17.41) * mm});
            skLineSegment(sketch, "E326", {"start": v(-62, 17.41) * mm, "end": v(-62, -17.41) * mm});
            skLineSegment(sketch, "E327", {"start": v(-62, -17.41) * mm, "end": v(-45.5, -17.41) * mm});
            skLineSegment(sketch, "E328.0", {"start": v(-59, -14.41) * mm, "end": v(-45.5, -14.41) * mm});
            skLineSegment(sketch, "E328.1", {"start": v(-59, 14.41) * mm, "end": v(-59, -14.41) * mm});
            skLineSegment(sketch, "E328.2", {"start": v(-45.5, 14.41) * mm, "end": v(-59, 14.41) * mm});
            skLineSegment(sketch, "E329.0", {"start": v(-42.5, 17.41) * mm, "end": v(-42.5, -17.41) * mm});
            skSolve(sketch);
        }
        {
            var Q0;
            Q0=makeQuery(id+"F8.imprint","IMPRINT",FACE,{"disambiguationData":[TD([[makeQuery(id+"F8.imprint","IMPRINT",EDGE,{"derivedFrom":sQuery(id+"F8.wireOp",EDGE,"E1.0")}),1.0]])]});
            extrude(context, id + "F15", {"entities" : qUnion([Q0]), "depth" : 7 * mm});
        }
        {
            var Q0;
            Q0=makeQuery(id+"F8.imprint","IMPRINT",FACE,{"disambiguationData":[TD([[makeQuery(id+"F8.imprint","IMPRINT",EDGE,{"derivedFrom":sQuery(id+"F8.wireOp",EDGE,"E50")}),-1.0]])]});
            var Q1;
            Q1=makeQuery(id+"F8.imprint","IMPRINT",FACE,{"disambiguationData":[TD([[makeQuery(id+"F8.imprint","IMPRINT",EDGE,{"derivedFrom":sQuery(id+"F8.wireOp",EDGE,"E43.MirrorCS")}),-1.0]])]});
            var Q2;
            Q2=makeQuery(id+"F8.imprint","IMPRINT",FACE,{"disambiguationData":[TD([[makeQuery(id+"F8.imprint","IMPRINT",EDGE,{"derivedFrom":sQuery(id+"F8.wireOp",EDGE,"E42.MirrorCS")}),-1.0]])]});
            var Q3;
            Q3=makeQuery(id+"F8.imprint","IMPRINT",FACE,{"disambiguationData":[TD([[makeQuery(id+"F8.imprint","IMPRINT",EDGE,{"derivedFrom":sQuery(id+"F8.wireOp",EDGE,"E41.MirrorCS")}),-1.0]])]});
            var Q4;
            Q4=makeQuery(id+"F8.imprint","IMPRINT",FACE,{"disambiguationData":[TD([[makeQuery(id+"F8.imprint","IMPRINT",EDGE,{"derivedFrom":sQuery(id+"F8.wireOp",EDGE,"E40.MirrorCS")}),1.0]])]});
            var Q5;
            Q5=makeQuery(id+"F8.imprint","IMPRINT",FACE,{"disambiguationData":[TD([[makeQuery(id+"F8.imprint","IMPRINT",EDGE,{"derivedFrom":sQuery(id+"F8.wireOp",EDGE,"E39.MirrorCS")}),-1.0]])]});
            var Q6;
            Q6=makeQuery(id+"F8.imprint","IMPRINT",FACE,{"disambiguationData":[TD([[makeQuery(id+"F8.imprint","IMPRINT",EDGE,{"derivedFrom":sQuery(id+"F8.wireOp",EDGE,"E27")}),1.0]])]});
            var Q7;
            Q7=makeQuery(id+"F8.imprint","IMPRINT",FACE,{"disambiguationData":[TD([[makeQuery(id+"F8.imprint","IMPRINT",EDGE,{"derivedFrom":sQuery(id+"F8.wireOp",EDGE,"E28")}),-1.0]])]});
            var Q8;
            Q8=makeQuery(id+"F8.imprint","IMPRINT",FACE,{"disambiguationData":[TD([[makeQuery(id+"F8.imprint","IMPRINT",EDGE,{"derivedFrom":sQuery(id+"F8.wireOp",EDGE,"E29")}),1.0]])]});
            var Q9;
            Q9=makeQuery(id+"F8.imprint","IMPRINT",FACE,{"disambiguationData":[TD([[makeQuery(id+"F8.imprint","IMPRINT",EDGE,{"derivedFrom":sQuery(id+"F8.wireOp",EDGE,"E30")}),-1.0]])]});
            var Q10;
            Q10=makeQuery(id+"F8.imprint","IMPRINT",FACE,{"disambiguationData":[TD([[makeQuery(id+"F8.imprint","IMPRINT",EDGE,{"derivedFrom":sQuery(id+"F8.wireOp",EDGE,"E31")}),-1.0]])]});
            var Q11;
            Q11=makeQuery(id+"F8.imprint","IMPRINT",FACE,{"disambiguationData":[TD([[makeQuery(id+"F8.imprint","IMPRINT",EDGE,{"derivedFrom":sQuery(id+"F8.wireOp",EDGE,"E32")}),-1.0]])]});
            var Q12;
            Q12=makeQuery(id+"F8.imprint","IMPRINT",FACE,{"disambiguationData":[TD([[makeQuery(id+"F8.imprint","IMPRINT",EDGE,{"derivedFrom":sQuery(id+"F8.wireOp",EDGE,"E33")}),-1.0]])]});
            var Q13;
            Q13=makeQuery(id+"F8.imprint","IMPRINT",FACE,{"disambiguationData":[TD([[makeQuery(id+"F8.imprint","IMPRINT",EDGE,{"derivedFrom":sQuery(id+"F8.wireOp",EDGE,"E34.MirrorCS")}),-1.0]])]});
            var Q14;
            Q14=makeQuery(id+"F8.imprint","IMPRINT",FACE,{"disambiguationData":[TD([[makeQuery(id+"F8.imprint","IMPRINT",EDGE,{"derivedFrom":sQuery(id+"F8.wireOp",EDGE,"E35.MirrorCS")}),-1.0]])]});
            var Q15;
            Q15=makeQuery(id+"F8.imprint","IMPRINT",FACE,{"disambiguationData":[TD([[makeQuery(id+"F8.imprint","IMPRINT",EDGE,{"derivedFrom":sQuery(id+"F8.wireOp",EDGE,"E36.MirrorCS")}),-1.0]])]});
            var Q16;
            Q16=makeQuery(id+"F8.imprint","IMPRINT",FACE,{"disambiguationData":[TD([[makeQuery(id+"F8.imprint","IMPRINT",EDGE,{"derivedFrom":sQuery(id+"F8.wireOp",EDGE,"E37.MirrorCS")}),1.0]])]});
            var Q17;
            Q17=makeQuery(id+"F8.imprint","IMPRINT",FACE,{"disambiguationData":[TD([[makeQuery(id+"F8.imprint","IMPRINT",EDGE,{"derivedFrom":sQuery(id+"F8.wireOp",EDGE,"E38.MirrorCS")}),-1.0]])]});
            var Q18;
            Q18=makeQuery(id+"F8.imprint","IMPRINT",FACE,{"disambiguationData":[TD([[makeQuery(id+"F8.imprint","IMPRINT",EDGE,{"derivedFrom":sQuery(id+"F8.wireOp",EDGE,"E49")}),-1.0]])]});
            var Q19;
            Q19=makeQuery(id+"F8.imprint","IMPRINT",FACE,{"disambiguationData":[TD([[makeQuery(id+"F8.imprint","IMPRINT",EDGE,{"derivedFrom":sQuery(id+"F8.wireOp",EDGE,"E48.MirrorCS")}),-1.0]])]});
            var Q20;
            Q20=makeQuery(id+"F8.imprint","IMPRINT",FACE,{"disambiguationData":[TD([[makeQuery(id+"F8.imprint","IMPRINT",EDGE,{"derivedFrom":sQuery(id+"F8.wireOp",EDGE,"E47.MirrorCS")}),1.0]])]});
            var Q21;
            Q21=makeQuery(id+"F8.imprint","IMPRINT",FACE,{"disambiguationData":[TD([[makeQuery(id+"F8.imprint","IMPRINT",EDGE,{"derivedFrom":sQuery(id+"F8.wireOp",EDGE,"E46.MirrorCS")}),-1.0]])]});
            var Q22;
            Q22=makeQuery(id+"F8.imprint","IMPRINT",FACE,{"disambiguationData":[TD([[makeQuery(id+"F8.imprint","IMPRINT",EDGE,{"derivedFrom":sQuery(id+"F8.wireOp",EDGE,"E45.MirrorCS")}),-1.0]])]});
            var Q23;
            Q23=makeQuery(id+"F8.imprint","IMPRINT",FACE,{"disambiguationData":[TD([[makeQuery(id+"F8.imprint","IMPRINT",EDGE,{"derivedFrom":sQuery(id+"F8.wireOp",EDGE,"E44.MirrorCS")}),-1.0]])]});
            extrude(context, id + "F16", {"entities" : qUnion([Q0, Q1, Q2, Q3, Q4, Q5, Q6, Q7, Q8, Q9, Q10, Q11, Q12, Q13, Q14, Q15, Q16, Q17, Q18, Q19, Q20, Q21, Q22, Q23]), "operationType" : NewBodyOperationType.ADD, "depth" : 2 * mm});
        }
        {
            var Q0;
            {var subQ0=sQuery(id+"F9.wireOp",EDGE,"E164");Q0=makeQuery(id+"F9.imprint","IMPRINT",FACE,{"disambiguationData":[TD([[makeQuery(id+"F9.imprint","IMPRINT",EDGE,{"derivedFrom":subQ0}),-1.0]])]});}
            var Q1;
            {var subQ0=sQuery(id+"F9.wireOp",EDGE,"E152");Q1=makeQuery(id+"F9.imprint","IMPRINT",FACE,{"disambiguationData":[TD([[makeQuery(id+"F9.imprint","IMPRINT",EDGE,{"derivedFrom":subQ0}),1.0]])]});}
            var Q2;
            Q2=sQuery(id+"F9.wireOp",EDGE,"E161");
            revolve(context, id + "F17", {"operationType" : NewBodyOperationType.ADD, "entities" : qUnion([Q0, Q1]), "axis" : qUnion([Q2]), "revolveType" : RevolveType.SYMMETRIC, "angle" : 315 * degree});
        }
        {
            var Q0;
            {var subQ3=sQuery(id+"F9.wireOp",EDGE,"E157");Q0=makeQuery(id+"F9.imprint","IMPRINT",FACE,{"disambiguationData":[TD([[makeQuery(id+"F9.imprint","IMPRINT",EDGE,{"derivedFrom":subQ3}),1.0]])]});}
            var Q1;
            Q1=makeQuery(id+"F9.imprint","IMPRINT",FACE,{"disambiguationData":[TD([[makeQuery(id+"F9.imprint","IMPRINT",EDGE,{"derivedFrom":sQuery(id+"F9.wireOp",EDGE,"E158")}),-1.0]])]});
            var Q2;
            Q2=sQuery(id+"F9.wireOp",EDGE,"E161");
            revolve(context, id + "F18", {"operationType" : NewBodyOperationType.ADD, "entities" : qUnion([Q0, Q1]), "axis" : qUnion([Q2]), "revolveType" : RevolveType.FULL});
        }
        {
            var Q0;
            Q0=makeQuery(id+"F12.imprint","IMPRINT",FACE,{"disambiguationData":[TD([[makeQuery(id+"F12.imprint","IMPRINT",EDGE,{"derivedFrom":sQuery(id+"F12.wireOp",EDGE,"E285")}),-1.0]])]});
            extrude(context, id + "F19", {"entities" : qUnion([Q0]), "operationType" : NewBodyOperationType.ADD, "depth" : 2.5 * mm});
        }
        {
            var Q0;
            Q0=makeQuery(id+"F11.imprint","IMPRINT",FACE,{"disambiguationData":[TD([[makeQuery(id+"F11.imprint","IMPRINT",EDGE,{"derivedFrom":sQuery(id+"F11.wireOp",EDGE,"E259")}),-1.0]])]});
            extrude(context, id + "F20", {"entities" : qUnion([Q0]), "operationType" : NewBodyOperationType.ADD, "oppositeDirection" : true, "depth" : 2.5 * mm});
        }
        {
            var Q0;
            Q0=makeQuery(id+"F13.imprint","IMPRINT",FACE,{"disambiguationData":[TD([[makeQuery(id+"F13.imprint","IMPRINT",EDGE,{"derivedFrom":sQuery(id+"F13.wireOp",EDGE,"E295.MirrorCS")}),1.0]])]});
            var Q1;
            {var subQ1=sQuery(id+"F13.wireOp",EDGE,"E299.bottom");Q1=makeQuery(id+"F13.imprint","IMPRINT",FACE,{"disambiguationData":[TD([[makeQuery(id+"F13.imprint","IMPRINT",EDGE,{"derivedFrom":subQ1}),1.0]])]});}
            var Q2;
            {var subQ5=sQuery(id+"F13.wireOp",EDGE,"E301");Q2=makeQuery(id+"F13.imprint","IMPRINT",FACE,{"disambiguationData":[TD([[makeQuery(id+"F13.imprint","IMPRINT",EDGE,{"derivedFrom":subQ5}),-1.0]])]});}
            var Q3;
            {var subQ0=sQuery(id+"F13.wireOp",EDGE,"E310.0");Q3=makeQuery(id+"F13.imprint","IMPRINT",FACE,{"disambiguationData":[TD([[makeQuery(id+"F13.imprint","IMPRINT",EDGE,{"derivedFrom":subQ0}),1.0]])]});}
            extrude(context, id + "F21", {"entities" : qUnion([Q0, Q1, Q2, Q3]), "operationType" : NewBodyOperationType.ADD, "depth" : 2.5 * mm});
        }
        {
            var Q0;
            {var subQ3=sQuery(id+"F14.wireOp",EDGE,"E313.MirrorCS");Q0=makeQuery(id+"F14.imprint","IMPRINT",FACE,{"disambiguationData":[TD([[makeQuery(id+"F14.imprint","IMPRINT",EDGE,{"derivedFrom":subQ3}),1.0]])]});}
            var Q1;
            {var subQ7=sQuery(id+"F14.wireOp",EDGE,"E329.0");Q1=makeQuery(id+"F14.imprint","IMPRINT",FACE,{"disambiguationData":[TD([[makeQuery(id+"F14.imprint","IMPRINT",EDGE,{"derivedFrom":subQ7}),-1.0]])]});}
            extrude(context, id + "F22", {"entities" : qUnion([Q0, Q1]), "operationType" : NewBodyOperationType.ADD, "oppositeDirection" : true, "depth" : 2.5 * mm});
        }
        {
            var Q0;
            {var subQ4=sQuery(id+"F13.wireOp",EDGE,"E301");Q0=makeQuery(id+"F13.imprint","IMPRINT",FACE,{"disambiguationData":[TD([[makeQuery(id+"F13.imprint","IMPRINT",EDGE,{"derivedFrom":subQ4}),1.0]])]});}
            var Q1;
            {var subQ0=sQuery(id+"F13.wireOp",EDGE,"6jEM1cKR-Vwea-ILg7-sG8q-rrc46WkZxeoR");Q1=makeQuery(id+"F13.imprint","IMPRINT",FACE,{"disambiguationData":[TD([[makeQuery(id+"F13.imprint","IMPRINT",EDGE,{"derivedFrom":subQ0}),-1.0]])]});}
            var Q2;
            {var subQ0=sQuery(id+"F13.wireOp",EDGE,"E307");Q2=makeQuery(id+"F13.imprint","IMPRINT",FACE,{"disambiguationData":[TD([[makeQuery(id+"F13.imprint","IMPRINT",EDGE,{"derivedFrom":subQ0}),1.0]])]});}
            extrude(context, id + "F23", {"entities" : qUnion([Q0, Q1, Q2]), "operationType" : NewBodyOperationType.ADD, "depth" : 14 * mm});
        }
        {
            var Q0;
            {var subQ0=sQuery(id+"F14.wireOp",EDGE,"E325");Q0=makeQuery(id+"F14.imprint","IMPRINT",FACE,{"disambiguationData":[TD([[makeQuery(id+"F14.imprint","IMPRINT",EDGE,{"derivedFrom":subQ0}),1.0]])]});}
            extrude(context, id + "F24", {"entities" : qUnion([Q0]), "operationType" : NewBodyOperationType.ADD, "depth" : 43.17 * mm});
        }
        {
            var Q0;
            Q0=makeQuery(id+"F10.imprint","IMPRINT",FACE,{"disambiguationData":[TD([[makeQuery(id+"F10.imprint","IMPRINT",EDGE,{"derivedFrom":sQuery(id+"F10.wireOp",EDGE,"E204")}),-1.0]])]});
            var Q1;
            {var subQ0=sQuery(id+"F10.wireOp",EDGE,"6a0bf37f-b3f9-4be4-bbcd-48762ca18b15");Q1=makeQuery(id+"F10.imprint","IMPRINT",FACE,{"disambiguationData":[TD([[makeQuery(id+"F10.imprint","IMPRINT",EDGE,{"derivedFrom":subQ0}),-1.0]])]});}
            var Q2;
            Q2=makeQuery(id+"F10.imprint","IMPRINT",FACE,{"disambiguationData":[TD([[makeQuery(id+"F10.imprint","IMPRINT",EDGE,{"derivedFrom":sQuery(id+"F10.wireOp",EDGE,"E204")}),1.0]])]});
            var Q3;
            Q3=makeQuery(id+"F10.imprint","IMPRINT",FACE,{"disambiguationData":[TD([[makeQuery(id+"F10.imprint","IMPRINT",EDGE,{"derivedFrom":sQuery(id+"F10.wireOp",EDGE,"E205.1")}),-1.0]])]});
            var Q4;
            {var subQ0=sQuery(id+"F10.wireOp",EDGE,"36538cae-b972-4159-a8ab-ed7d0897e562");Q4=makeQuery(id+"F10.imprint","IMPRINT",FACE,{"disambiguationData":[TD([[makeQuery(id+"F10.imprint","IMPRINT",EDGE,{"derivedFrom":subQ0}),1.0]])]});}
            var Q5;
            Q5=makeQuery(id+"F10.imprint","IMPRINT",FACE,{"disambiguationData":[TD([[makeQuery(id+"F10.imprint","IMPRINT",EDGE,{"derivedFrom":sQuery(id+"F10.wireOp",EDGE,"E203.MirrorCS")}),-1.0]])]});
            var Q6;
            Q6=makeQuery(id+"F10.imprint","IMPRINT",FACE,{"disambiguationData":[TD([[makeQuery(id+"F10.imprint","IMPRINT",EDGE,{"derivedFrom":sQuery(id+"F10.wireOp",EDGE,"E202.0")}),1.0]])]});
            var Q7;
            {var subQ2=sQuery(id+"F10.wireOp",EDGE,"E232.MirrorCS");Q7=makeQuery(id+"F10.imprint","IMPRINT",FACE,{"disambiguationData":[TD([[makeQuery(id+"F10.imprint","IMPRINT",EDGE,{"derivedFrom":subQ2}),1.0]])]});}
            var Q8;
            {var subQ0=sQuery(id+"F10.wireOp",EDGE,"E215");Q8=makeQuery(id+"F10.imprint","IMPRINT",FACE,{"disambiguationData":[TD([[makeQuery(id+"F10.imprint","IMPRINT",EDGE,{"derivedFrom":subQ0}),-1.0]])]});}
            var Q9;
            {var subQ2=sQuery(id+"F10.wireOp",EDGE,"E230");Q9=makeQuery(id+"F10.imprint","IMPRINT",FACE,{"disambiguationData":[TD([[makeQuery(id+"F10.imprint","IMPRINT",EDGE,{"derivedFrom":subQ2}),-1.0]])]});}
            extrude(context, id + "F25", {"entities" : qUnion([Q0, Q1, Q2, Q3, Q4, Q5, Q6, Q7, Q8, Q9]), "operationType" : NewBodyOperationType.ADD, "oppositeDirection" : true, "depth" : 3 * mm});
        }
        {
            var Q0;
            {var subQ1=sQuery(id+"F10.wireOp",EDGE,"E223.MirrorCS");Q0=makeQuery(id+"F10.imprint","IMPRINT",FACE,{"disambiguationData":[TD([[makeQuery(id+"F10.imprint","IMPRINT",EDGE,{"derivedFrom":subQ1}),-1.0]])]});}
            var Q1;
            {var subQ0=sQuery(id+"F10.wireOp",EDGE,"E229");var subQ1=sQuery(id+"F10.wireOp",EDGE,"E219");var subQ2=makeQuery(id+"F10.imprint","INTERSECT",VERTEX,{"disambiguationData":[OD(0.0)],"derivedFrom":[subQ1,subQ0]});Q1=makeQuery(id+"F10.imprint","IMPRINT",FACE,{"disambiguationData":[TD([[makeQuery(id+"F10.imprint","IMPRINT",EDGE,{"disambiguationData":[TD([[subQ2,-1.0]])],"derivedFrom":subQ1}),-1.0]])]});}
            var Q2;
            {var subQ0=sQuery(id+"F10.wireOp",EDGE,"E229");var subQ1=sQuery(id+"F10.wireOp",EDGE,"E219");var subQ2=makeQuery(id+"F10.imprint","INTERSECT",VERTEX,{"disambiguationData":[OD(1.0)],"derivedFrom":[subQ1,subQ0]});Q2=makeQuery(id+"F10.imprint","IMPRINT",FACE,{"disambiguationData":[TD([[makeQuery(id+"F10.imprint","IMPRINT",EDGE,{"disambiguationData":[TD([[subQ2,1.0]])],"derivedFrom":subQ1}),-1.0]])]});}
            var Q3;
            {var subQ0=sQuery(id+"F10.wireOp",EDGE,"E222.1");Q3=makeQuery(id+"F10.imprint","IMPRINT",FACE,{"disambiguationData":[TD([[makeQuery(id+"F10.imprint","IMPRINT",EDGE,{"derivedFrom":subQ0}),1.0]])]});}
            var Q4;
            Q4=makeQuery(id+"F10.imprint","IMPRINT",FACE,{"disambiguationData":[TD([[makeQuery(id+"F10.imprint","IMPRINT",EDGE,{"derivedFrom":sQuery(id+"F10.wireOp",EDGE,"E202.0")}),-1.0]])]});
            extrude(context, id + "F26", {"entities" : qUnion([Q0, Q1, Q2, Q3, Q4]), "operationType" : NewBodyOperationType.ADD, "endBound" : BoundingType.SYMMETRIC, "depth" : 3 * mm});
        }
        {
            var Q0;
            {var subQ0=sQuery(id+"F10.wireOp",EDGE,"E229");var subQ1=sQuery(id+"F10.wireOp",EDGE,"E219");var subQ2=makeQuery(id+"F10.imprint","INTERSECT",VERTEX,{"disambiguationData":[OD(1.0)],"derivedFrom":[subQ1,subQ0]});Q0=makeQuery(id+"F10.imprint","IMPRINT",FACE,{"disambiguationData":[TD([[makeQuery(id+"F10.imprint","IMPRINT",EDGE,{"disambiguationData":[TD([[subQ2,1.0]])],"derivedFrom":subQ1}),-1.0]])]});}
            var Q1;
            {var subQ0=sQuery(id+"F10.wireOp",EDGE,"E229");var subQ1=sQuery(id+"F10.wireOp",EDGE,"E219");var subQ2=makeQuery(id+"F10.imprint","INTERSECT",VERTEX,{"disambiguationData":[OD(0.0)],"derivedFrom":[subQ1,subQ0]});Q1=makeQuery(id+"F10.imprint","IMPRINT",FACE,{"disambiguationData":[TD([[makeQuery(id+"F10.imprint","IMPRINT",EDGE,{"disambiguationData":[TD([[subQ2,-1.0]])],"derivedFrom":subQ1}),-1.0]])]});}
            extrude(context, id + "F27", {"entities" : qUnion([Q0, Q1]), "operationType" : NewBodyOperationType.ADD, "depth" : 3.5 * mm});
        }
        {
            var Q0;
            Q0=makeQuery(id+"F10.imprint","IMPRINT",FACE,{"disambiguationData":[TD([[makeQuery(id+"F10.imprint","IMPRINT",EDGE,{"derivedFrom":sQuery(id+"F10.wireOp",EDGE,"E203.MirrorCS")}),-1.0]])]});
            var Q1;
            Q1=makeQuery(id+"F10.imprint","IMPRINT",FACE,{"disambiguationData":[TD([[makeQuery(id+"F10.imprint","IMPRINT",EDGE,{"derivedFrom":sQuery(id+"F10.wireOp",EDGE,"E204")}),1.0]])]});
            var Q2;
            Q2=makeQuery(id+"F10.imprint","IMPRINT",FACE,{"disambiguationData":[TD([[makeQuery(id+"F10.imprint","IMPRINT",EDGE,{"derivedFrom":sQuery(id+"F10.wireOp",EDGE,"E202.0")}),1.0]])]});
            var Q3;
            Q3=makeQuery(id+"F10.imprint","IMPRINT",FACE,{"disambiguationData":[TD([[makeQuery(id+"F10.imprint","IMPRINT",EDGE,{"derivedFrom":sQuery(id+"F10.wireOp",EDGE,"E205.1")}),-1.0]])]});
            extrude(context, id + "F28", {"entities" : qUnion([Q0, Q1, Q2, Q3]), "operationType" : NewBodyOperationType.ADD, "depth" : 8.2 * mm});
        }
        {
            var Q0;
            Q0=qCreatedBy(id+"F6.planeOp",FACE);
            var sketch = newSketch(context, id + "F29", { "sketchPlane" : qUnion([Q0])});
            skCircle(sketch, "E330", {"center": v(0, 0) * mm, "radius": 1.5 * mm, "construction": true});
            skCircle(sketch, "E331", {"center": v(0, 50.8) * mm, "radius": 1.25 * mm, "construction": true});
            skLineSegment(sketch, "E332", {"start": v(0, 55.8) * mm, "end": v(0, 14) * mm, "construction": true});
            skSolve(sketch);
        }
        {
            var Q0;
            Q0=qCreatedBy(id+"F5.planeOp",FACE);
            var sketch = newSketch(context, id + "F30", { "sketchPlane" : qUnion([Q0])});
            skPoint(sketch, "E333.middle", {"position": v(0, 0) * mm});
            skCircle(sketch, "E334", {"center": v(0, 0) * mm, "radius": 1.5 * mm, "construction": true});
            skLineSegment(sketch, "E335.bottom", {"start": v(-45.5, 8.28) * mm, "end": v(-45.5, -8.52) * mm, "construction": true});
            skLineSegment(sketch, "E335.left", {"start": v(-45.5, 8.28) * mm, "end": v(-59, 8.28) * mm, "construction": true});
            skLineSegment(sketch, "E336", {"start": v(-45.5, -8.52) * mm, "end": v(-59, -8.52) * mm, "construction": true});
            skLineSegment(sketch, "E337", {"start": v(-59, -8.52) * mm, "end": v(-59, 8.28) * mm, "construction": true});
            skLineSegment(sketch, "E338", {"start": v(-45.5, 8.28) * mm, "end": v(-59, -8.52) * mm, "construction": true});
            skLineSegment(sketch, "E339", {"start": v(-45.5, -8.52) * mm, "end": v(-59, 8.28) * mm, "construction": true});
            skLineSegment(sketch, "E340", {"start": v(-52.24, 0) * mm, "end": v(-42.5, 0) * mm, "construction": true});
            skLineSegment(sketch, "E341", {"start": v(-27.2, 0) * mm, "end": v(-42.4, 0) * mm, "construction": true});
            skLineSegment(sketch, "E342.0", {"start": v(-62, -8.52) * mm, "end": v(-62, 8.28) * mm, "construction": true});
            skLineSegment(sketch, "E343", {"start": v(-62, 17.41) * mm, "end": v(-62, -17.41) * mm});
            skLineSegment(sketch, "E344.0", {"start": v(-59, -14.41) * mm, "end": v(-45.5, -14.41) * mm, "construction": true});
            skLineSegment(sketch, "E344.1", {"start": v(-59, 14.41) * mm, "end": v(-59, -14.41) * mm});
            skLineSegment(sketch, "E344.2", {"start": v(-45.5, 14.41) * mm, "end": v(-59, 14.41) * mm, "construction": true});
            skLineSegment(sketch, "E345.0", {"start": v(-42.5, 17.41) * mm, "end": v(-42.5, -17.41) * mm});
            skLineSegment(sketch, "E346", {"start": v(-62, 17.41) * mm, "end": v(-42.5, 17.41) * mm});
            skLineSegment(sketch, "E347", {"start": v(-42.5, -17.41) * mm, "end": v(-62, -17.41) * mm});
            skLineSegment(sketch, "E348", {"start": v(-45.5, 14.41) * mm, "end": v(-45.5, -14.41) * mm});
            skLineSegment(sketch, "E349", {"start": v(-62, 14.41) * mm, "end": v(-42.5, 14.41) * mm});
            skLineSegment(sketch, "E350", {"start": v(-42.5, -14.41) * mm, "end": v(-62, -14.41) * mm});
            skPoint(sketch, "E350.endSnap0", {"position": v(-52.25, -14.41) * mm});
            skSolve(sketch);
        }
        {
            var Q0;
            Q0=qCreatedBy(id+"F7.planeOp",FACE);
            var sketch = newSketch(context, id + "F31", { "sketchPlane" : qUnion([Q0])});
            skPoint(sketch, "E351.middle", {"position": v(-3, 0) * mm});
            skLineSegment(sketch, "E352.bottom", {"start": v(-48.5, 8.28) * mm, "end": v(-48.5, -8.52) * mm, "construction": true});
            skLineSegment(sketch, "E352.left", {"start": v(-48.5, 8.28) * mm, "end": v(-62, 8.28) * mm, "construction": true});
            skLineSegment(sketch, "E353", {"start": v(-48.5, -8.52) * mm, "end": v(-62, -8.52) * mm, "construction": true});
            skLineSegment(sketch, "E354", {"start": v(-62, -8.52) * mm, "end": v(-62, 8.28) * mm, "construction": true});
            skLineSegment(sketch, "E355", {"start": v(-48.5, 8.28) * mm, "end": v(-62, -8.52) * mm, "construction": true});
            skLineSegment(sketch, "E356", {"start": v(-48.5, -8.52) * mm, "end": v(-62, 8.28) * mm, "construction": true});
            skLineSegment(sketch, "E357", {"start": v(-55.24, 0) * mm, "end": v(-45.5, 0) * mm, "construction": true});
            skLineSegment(sketch, "E358", {"start": v(-30.2, 0) * mm, "end": v(-45.4, 0) * mm, "construction": true});
            skLineSegment(sketch, "E359.0", {"start": v(-65, -8.52) * mm, "end": v(-65, 8.28) * mm, "construction": true});
            skLineSegment(sketch, "E360", {"start": v(-65, 17.41) * mm, "end": v(-65, -17.41) * mm});
            skLineSegment(sketch, "E361.0", {"start": v(-62, -14.41) * mm, "end": v(-48.5, -14.41) * mm, "construction": true});
            skLineSegment(sketch, "E361.1", {"start": v(-62, 14.41) * mm, "end": v(-62, -14.41) * mm});
            skLineSegment(sketch, "E361.2", {"start": v(-48.5, 14.41) * mm, "end": v(-62, 14.41) * mm, "construction": true});
            skLineSegment(sketch, "E362.0", {"start": v(-45.5, 17.41) * mm, "end": v(-45.5, -17.41) * mm});
            skLineSegment(sketch, "E363", {"start": v(-65, 17.41) * mm, "end": v(-45.5, 17.41) * mm});
            skLineSegment(sketch, "E364", {"start": v(-45.5, -17.41) * mm, "end": v(-65, -17.41) * mm});
            skCircle(sketch, "E365", {"center": v(0, 0) * mm, "radius": 3 * mm, "construction": true});
            skLineSegment(sketch, "E366", {"start": v(-48.5, 14.41) * mm, "end": v(-48.5, -14.41) * mm});
            skLineSegment(sketch, "E367", {"start": v(-65, 14.41) * mm, "end": v(-45.5, 14.41) * mm});
            skLineSegment(sketch, "E368", {"start": v(-45.5, -14.41) * mm, "end": v(-65, -14.41) * mm});
            skSolve(sketch);
        }
        {
            var Q0;
            Q0=sQuery(id+"F29.wireOp",VERTEX,"E331.center");
            var Q1;
            Q1=makeQuery(id+"F15.opExtrude","SWEPT_BODY",BODY,{"disambiguationData":[OSD([sQuery(id+"F8.wireOp",EDGE,"E1.0"),sQuery(id+"F8.wireOp",EDGE,"E27"),sQuery(id+"F8.wireOp",EDGE,"E28"),sQuery(id+"F8.wireOp",EDGE,"E29"),sQuery(id+"F8.wireOp",EDGE,"E30"),sQuery(id+"F8.wireOp",EDGE,"E31"),sQuery(id+"F8.wireOp",EDGE,"E32"),sQuery(id+"F8.wireOp",EDGE,"E33"),sQuery(id+"F8.wireOp",EDGE,"E34.MirrorCS"),sQuery(id+"F8.wireOp",EDGE,"E35.MirrorCS"),sQuery(id+"F8.wireOp",EDGE,"E36.MirrorCS"),sQuery(id+"F8.wireOp",EDGE,"E37.MirrorCS"),sQuery(id+"F8.wireOp",EDGE,"E38.MirrorCS"),sQuery(id+"F8.wireOp",EDGE,"E39.MirrorCS"),sQuery(id+"F8.wireOp",EDGE,"E40.MirrorCS"),sQuery(id+"F8.wireOp",EDGE,"E41.MirrorCS"),sQuery(id+"F8.wireOp",EDGE,"E42.MirrorCS"),sQuery(id+"F8.wireOp",EDGE,"E43.MirrorCS"),sQuery(id+"F8.wireOp",EDGE,"E44.MirrorCS"),sQuery(id+"F8.wireOp",EDGE,"E45.MirrorCS"),sQuery(id+"F8.wireOp",EDGE,"E46.MirrorCS"),sQuery(id+"F8.wireOp",EDGE,"E47.MirrorCS"),sQuery(id+"F8.wireOp",EDGE,"E48.MirrorCS"),sQuery(id+"F8.wireOp",EDGE,"E49"),sQuery(id+"F8.wireOp",EDGE,"E50"),sQuery(id+"F8.wireOp",EDGE,"E51"),sQuery(id+"F8.wireOp",EDGE,"E52"),sQuery(id+"F8.wireOp",EDGE,"E53"),sQuery(id+"F8.wireOp",EDGE,"E54"),sQuery(id+"F8.wireOp",EDGE,"E55"),sQuery(id+"F8.wireOp",EDGE,"E56"),sQuery(id+"F8.wireOp",EDGE,"E57"),sQuery(id+"F8.wireOp",EDGE,"E58.MirrorCS"),sQuery(id+"F8.wireOp",EDGE,"E59.MirrorCS"),sQuery(id+"F8.wireOp",EDGE,"E60.MirrorCS"),sQuery(id+"F8.wireOp",EDGE,"E61.MirrorCS"),sQuery(id+"F8.wireOp",EDGE,"E62.MirrorCS"),sQuery(id+"F8.wireOp",EDGE,"E63.MirrorCS"),sQuery(id+"F8.wireOp",EDGE,"E64.MirrorCS"),sQuery(id+"F8.wireOp",EDGE,"E65.MirrorCS"),sQuery(id+"F8.wireOp",EDGE,"E66.MirrorCS"),sQuery(id+"F8.wireOp",EDGE,"E67.MirrorCS"),sQuery(id+"F8.wireOp",EDGE,"E68.MirrorCS"),sQuery(id+"F8.wireOp",EDGE,"E69.MirrorCS"),sQuery(id+"F8.wireOp",EDGE,"E70.MirrorCS"),sQuery(id+"F8.wireOp",EDGE,"E71.MirrorCS"),sQuery(id+"F8.wireOp",EDGE,"E72.MirrorCS"),sQuery(id+"F8.wireOp",EDGE,"E73"),sQuery(id+"F8.wireOp",EDGE,"E74"),sQuery(id+"F8.wireOp",EDGE,"E76"),sQuery(id+"F8.wireOp",EDGE,"E78"),sQuery(id+"F8.wireOp",EDGE,"E80"),sQuery(id+"F8.wireOp",EDGE,"E82"),sQuery(id+"F8.wireOp",EDGE,"E84"),sQuery(id+"F8.wireOp",EDGE,"E86"),sQuery(id+"F8.wireOp",EDGE,"E88"),sQuery(id+"F8.wireOp",EDGE,"E90"),sQuery(id+"F8.wireOp",EDGE,"E92"),sQuery(id+"F8.wireOp",EDGE,"E94"),sQuery(id+"F8.wireOp",EDGE,"E96"),sQuery(id+"F8.wireOp",EDGE,"E98"),sQuery(id+"F8.wireOp",EDGE,"E100"),sQuery(id+"F8.wireOp",EDGE,"E102"),sQuery(id+"F8.wireOp",EDGE,"E104"),sQuery(id+"F8.wireOp",EDGE,"E106"),sQuery(id+"F8.wireOp",EDGE,"E108"),sQuery(id+"F8.wireOp",EDGE,"E110"),sQuery(id+"F8.wireOp",EDGE,"E112"),sQuery(id+"F8.wireOp",EDGE,"E114"),sQuery(id+"F8.wireOp",EDGE,"E116"),sQuery(id+"F8.wireOp",EDGE,"E118"),sQuery(id+"F8.wireOp",EDGE,"E119"),sQuery(id+"F8.wireOp",EDGE,"E122"),sQuery(id+"F8.wireOp",EDGE,"E124"),sQuery(id+"F8.wireOp",EDGE,"E125"),sQuery(id+"F8.wireOp",EDGE,"E126"),sQuery(id+"F8.wireOp",EDGE,"E127"),sQuery(id+"F8.wireOp",EDGE,"E128"),sQuery(id+"F8.wireOp",EDGE,"E129"),sQuery(id+"F8.wireOp",EDGE,"E130"),sQuery(id+"F8.wireOp",EDGE,"E131"),sQuery(id+"F8.wireOp",EDGE,"E132"),sQuery(id+"F8.wireOp",EDGE,"E133"),sQuery(id+"F8.wireOp",EDGE,"E134"),sQuery(id+"F8.wireOp",EDGE,"E135"),sQuery(id+"F8.wireOp",EDGE,"E136"),sQuery(id+"F8.wireOp",EDGE,"E137"),sQuery(id+"F8.wireOp",EDGE,"E138"),sQuery(id+"F8.wireOp",EDGE,"E139"),sQuery(id+"F8.wireOp",EDGE,"E140"),sQuery(id+"F8.wireOp",EDGE,"E141"),sQuery(id+"F8.wireOp",EDGE,"E142"),sQuery(id+"F8.wireOp",EDGE,"E143"),sQuery(id+"F8.wireOp",EDGE,"E144"),sQuery(id+"F8.wireOp",EDGE,"E145"),sQuery(id+"F8.wireOp",EDGE,"E146"),sQuery(id+"F8.wireOp",EDGE,"E147")])]});
            hole(context, id + "F32", {"style" : HoleStyle.SIMPLE, "endStyle" : HoleEndStyle.BLIND, "oppositeDirection" : true, "holeDiameter" : 7 * mm, "holeDepth" : 4 * mm, "isTappedThrough" : true, "tappedDepth" : 12 * mm, "tapClearance" : 3, "startFromSketch" : true, "locations" : qUnion([Q0]), "scope" : qUnion([Q1])});
        }
        {
            var Q0;
            {var subQ4=sQuery(id+"F30.wireOp",EDGE,"E347");Q0=makeQuery(id+"F30.imprint","IMPRINT",FACE,{"disambiguationData":[TD([[makeQuery(id+"F30.imprint","IMPRINT",EDGE,{"derivedFrom":subQ4}),-1.0]])]});}
            var Q1;
            {var subQ4=sQuery(id+"F31.wireOp",EDGE,"E364");Q1=makeQuery(id+"F31.imprint","IMPRINT",FACE,{"disambiguationData":[TD([[makeQuery(id+"F31.imprint","IMPRINT",EDGE,{"derivedFrom":subQ4}),-1.0]])]});}
            loft(context, id + "F33", {"sheetProfilesArray" : [{ "sheetProfileEntities" : qUnion([Q0]) }, { "sheetProfileEntities" : qUnion([Q1]) }]});
        }
        {
            var Q1;
            {var subQ5=sQuery(id+"F30.wireOp",EDGE,"E348");Q1=makeQuery(id+"F30.imprint","IMPRINT",FACE,{"disambiguationData":[TD([[makeQuery(id+"F30.imprint","IMPRINT",EDGE,{"derivedFrom":subQ5}),1.0]])]});}
            var Q2;
            {var subQ5=sQuery(id+"F31.wireOp",EDGE,"E366");Q2=makeQuery(id+"F31.imprint","IMPRINT",FACE,{"disambiguationData":[TD([[makeQuery(id+"F31.imprint","IMPRINT",EDGE,{"derivedFrom":subQ5}),1.0]])]});}
            loft(context, id + "F34", {"operationType" : NewBodyOperationType.ADD, "sheetProfilesArray" : [{ "sheetProfileEntities" : qUnion([Q1]) }, { "sheetProfileEntities" : qUnion([Q2]) }]});
        }
        {
            var Q1;
            {var subQ0=sQuery(id+"F30.wireOp",EDGE,"E346");Q1=makeQuery(id+"F30.imprint","IMPRINT",FACE,{"disambiguationData":[TD([[makeQuery(id+"F30.imprint","IMPRINT",EDGE,{"derivedFrom":subQ0}),-1.0]])]});}
            var Q2;
            {var subQ0=sQuery(id+"F31.wireOp",EDGE,"E363");Q2=makeQuery(id+"F31.imprint","IMPRINT",FACE,{"disambiguationData":[TD([[makeQuery(id+"F31.imprint","IMPRINT",EDGE,{"derivedFrom":subQ0}),-1.0]])]});}
            loft(context, id + "F35", {"operationType" : NewBodyOperationType.ADD, "sheetProfilesArray" : [{ "sheetProfileEntities" : qUnion([Q1]) }, { "sheetProfileEntities" : qUnion([Q2]) }]});
        }
        {
            var Q1;
            {var subQ5=sQuery(id+"F30.wireOp",EDGE,"E344.1");Q1=makeQuery(id+"F30.imprint","IMPRINT",FACE,{"disambiguationData":[TD([[makeQuery(id+"F30.imprint","IMPRINT",EDGE,{"derivedFrom":subQ5}),-1.0]])]});}
            var Q2;
            {var subQ5=sQuery(id+"F31.wireOp",EDGE,"E361.1");Q2=makeQuery(id+"F31.imprint","IMPRINT",FACE,{"disambiguationData":[TD([[makeQuery(id+"F31.imprint","IMPRINT",EDGE,{"derivedFrom":subQ5}),-1.0]])]});}
            loft(context, id + "F36", {"operationType" : NewBodyOperationType.ADD, "sheetProfilesArray" : [{ "sheetProfileEntities" : qUnion([Q1]) }, { "sheetProfileEntities" : qUnion([Q2]) }]});
        }
        {
            var Q0;
            {var subQ0=sQuery(id+"F31.wireOp",EDGE,"E363");Q0=makeQuery(id+"F31.imprint","IMPRINT",FACE,{"disambiguationData":[TD([[makeQuery(id+"F31.imprint","IMPRINT",EDGE,{"derivedFrom":subQ0}),-1.0]])]});}
            var Q1;
            {var subQ5=sQuery(id+"F31.wireOp",EDGE,"E366");Q1=makeQuery(id+"F31.imprint","IMPRINT",FACE,{"disambiguationData":[TD([[makeQuery(id+"F31.imprint","IMPRINT",EDGE,{"derivedFrom":subQ5}),1.0]])]});}
            var Q2;
            {var subQ4=sQuery(id+"F31.wireOp",EDGE,"E364");Q2=makeQuery(id+"F31.imprint","IMPRINT",FACE,{"disambiguationData":[TD([[makeQuery(id+"F31.imprint","IMPRINT",EDGE,{"derivedFrom":subQ4}),-1.0]])]});}
            var Q3;
            {var subQ5=sQuery(id+"F31.wireOp",EDGE,"E361.1");Q3=makeQuery(id+"F31.imprint","IMPRINT",FACE,{"disambiguationData":[TD([[makeQuery(id+"F31.imprint","IMPRINT",EDGE,{"derivedFrom":subQ5}),-1.0]])]});}
            extrude(context, id + "F37", {"entities" : qUnion([Q0, Q1, Q2, Q3]), "operationType" : NewBodyOperationType.ADD, "depth" : 8 * mm});
        }
        {
            var Q0;
            {var subQ0=sQuery(id+"F8.wireOp",EDGE,"E145");var subQ1=sQuery(id+"F8.wireOp",EDGE,"E69.MirrorCS");var subQ2=sQuery(id+"F8.wireOp",EDGE,"E46.MirrorCS");var subQ3=makeQuery(id+"F16.opExtrude","CAP_FACE",FACE,{"disambiguationData":[OSD([subQ2,subQ1,sQuery(id+"F8.wireOp",EDGE,"E117"),subQ0])],"isStart":true});var subQ4=sQuery(id+"F12.wireOp",EDGE,"E290");var subQ5=sQuery(id+"F12.wireOp",EDGE,"E289");var subQ6=sQuery(id+"F12.wireOp",EDGE,"E288");var subQ7=sQuery(id+"F12.wireOp",EDGE,"E287");var subQ8=sQuery(id+"F12.wireOp",EDGE,"E286");var subQ9=sQuery(id+"F12.wireOp",EDGE,"E285");var subQ10=makeQuery(id+"F19.opExtrude","CAP_FACE",FACE,{"disambiguationData":[OSD([subQ9,subQ8,subQ7,subQ6,subQ5,subQ4])],"isStart":false});var subQ11=sQuery(id+"F8.wireOp",EDGE,"E146");var subQ12=sQuery(id+"F8.wireOp",EDGE,"E68.MirrorCS");var subQ13=sQuery(id+"F8.wireOp",EDGE,"E45.MirrorCS");var subQ14=makeQuery(id+"F16.opExtrude","CAP_FACE",FACE,{"disambiguationData":[OSD([subQ13,subQ12,sQuery(id+"F8.wireOp",EDGE,"E120"),subQ11])],"isStart":true});var subQ15=makeQuery(id+"F18.opRevolve","SWEPT_FACE",FACE,{"disambiguationData":[OSD([sQuery(id+"F9.wireOp",EDGE,"E157")])]});var subQ16=sQuery(id+"F8.wireOp",EDGE,"E147");var subQ17=sQuery(id+"F8.wireOp",EDGE,"E74");var subQ18=sQuery(id+"F8.wireOp",EDGE,"E44.MirrorCS");var subQ19=makeQuery(id+"F16.opExtrude","CAP_FACE",FACE,{"disambiguationData":[OSD([subQ18,subQ17,sQuery(id+"F8.wireOp",EDGE,"E121"),subQ16])],"isStart":true});var subQ20=sQuery(id+"F9.wireOp",EDGE,"E164");var subQ21=sQuery(id+"F9.wireOp",EDGE,"E152");var subQ22=sQuery(id+"F9.wireOp",EDGE,"E151");var subQ23=sQuery(id+"F9.wireOp",EDGE,"E150");var subQ24=makeQuery(id+"F17.opRevolve","CAP_FACE",FACE,{"disambiguationData":[OSD([subQ23,subQ22,subQ21,subQ20])],"isStart":false});var subQ25=sQuery(id+"F8.wireOp",EDGE,"E125");var subQ26=sQuery(id+"F8.wireOp",EDGE,"E66.MirrorCS");var subQ27=sQuery(id+"F8.wireOp",EDGE,"E43.MirrorCS");var subQ28=makeQuery(id+"F16.opExtrude","CAP_FACE",FACE,{"disambiguationData":[OSD([subQ27,subQ26,sQuery(id+"F8.wireOp",EDGE,"E77"),subQ25])],"isStart":true});var subQ29=sQuery(id+"F8.wireOp",EDGE,"E126");var subQ30=sQuery(id+"F8.wireOp",EDGE,"E65.MirrorCS");var subQ31=sQuery(id+"F8.wireOp",EDGE,"E42.MirrorCS");var subQ32=makeQuery(id+"F16.opExtrude","CAP_FACE",FACE,{"disambiguationData":[OSD([subQ31,subQ30,sQuery(id+"F8.wireOp",EDGE,"E79"),subQ29])],"isStart":true});var subQ33=sQuery(id+"F8.wireOp",EDGE,"E127");var subQ34=sQuery(id+"F8.wireOp",EDGE,"E64.MirrorCS");var subQ35=sQuery(id+"F8.wireOp",EDGE,"E41.MirrorCS");var subQ36=makeQuery(id+"F16.opExtrude","CAP_FACE",FACE,{"disambiguationData":[OSD([subQ35,subQ34,sQuery(id+"F8.wireOp",EDGE,"E81"),subQ33])],"isStart":true});var subQ37=sQuery(id+"F8.wireOp",EDGE,"E128");var subQ38=sQuery(id+"F8.wireOp",EDGE,"E63.MirrorCS");var subQ39=sQuery(id+"F8.wireOp",EDGE,"E40.MirrorCS");var subQ40=makeQuery(id+"F16.opExtrude","CAP_FACE",FACE,{"disambiguationData":[OSD([subQ39,subQ38,sQuery(id+"F8.wireOp",EDGE,"E83"),subQ37])],"isStart":true});var subQ41=sQuery(id+"F8.wireOp",EDGE,"E129");var subQ42=sQuery(id+"F8.wireOp",EDGE,"E51");var subQ43=sQuery(id+"F8.wireOp",EDGE,"E39.MirrorCS");var subQ44=makeQuery(id+"F16.opExtrude","CAP_FACE",FACE,{"disambiguationData":[OSD([subQ43,subQ42,sQuery(id+"F8.wireOp",EDGE,"E85"),subQ41])],"isStart":true});var subQ45=sQuery(id+"F8.wireOp",EDGE,"E141");var subQ46=sQuery(id+"F8.wireOp",EDGE,"E73");var subQ47=sQuery(id+"F8.wireOp",EDGE,"E38.MirrorCS");var subQ48=makeQuery(id+"F16.opExtrude","CAP_FACE",FACE,{"disambiguationData":[OSD([subQ47,subQ46,sQuery(id+"F8.wireOp",EDGE,"E109"),subQ45])],"isStart":true});var subQ49=sQuery(id+"F8.wireOp",EDGE,"E140");var subQ50=sQuery(id+"F8.wireOp",EDGE,"E62.MirrorCS");var subQ51=sQuery(id+"F8.wireOp",EDGE,"E37.MirrorCS");var subQ52=makeQuery(id+"F16.opExtrude","CAP_FACE",FACE,{"disambiguationData":[OSD([subQ51,subQ50,sQuery(id+"F8.wireOp",EDGE,"E107"),subQ49])],"isStart":true});var subQ53=sQuery(id+"F8.wireOp",EDGE,"E139");var subQ54=sQuery(id+"F8.wireOp",EDGE,"E61.MirrorCS");var subQ55=sQuery(id+"F8.wireOp",EDGE,"E36.MirrorCS");var subQ56=makeQuery(id+"F16.opExtrude","CAP_FACE",FACE,{"disambiguationData":[OSD([subQ55,subQ54,sQuery(id+"F8.wireOp",EDGE,"E105"),subQ53])],"isStart":true});var subQ57=sQuery(id+"F8.wireOp",EDGE,"E138");var subQ58=sQuery(id+"F8.wireOp",EDGE,"E60.MirrorCS");var subQ59=sQuery(id+"F8.wireOp",EDGE,"E35.MirrorCS");var subQ60=makeQuery(id+"F16.opExtrude","CAP_FACE",FACE,{"disambiguationData":[OSD([subQ59,subQ58,sQuery(id+"F8.wireOp",EDGE,"E103"),subQ57])],"isStart":true});var subQ61=sQuery(id+"F8.wireOp",EDGE,"E131");var subQ62=sQuery(id+"F8.wireOp",EDGE,"E53");var subQ63=sQuery(id+"F8.wireOp",EDGE,"E28");var subQ64=makeQuery(id+"F16.opExtrude","CAP_FACE",FACE,{"disambiguationData":[OSD([subQ63,subQ62,sQuery(id+"F8.wireOp",EDGE,"E89"),subQ61])],"isStart":true});var subQ65=makeQuery(id+"F17.opRevolve","CAP_FACE",FACE,{"disambiguationData":[OSD([subQ23,subQ22,subQ21,subQ20])],"isStart":true});var subQ66=sQuery(id+"F8.wireOp",EDGE,"E130");var subQ67=sQuery(id+"F8.wireOp",EDGE,"E52");var subQ68=sQuery(id+"F8.wireOp",EDGE,"E27");var subQ69=makeQuery(id+"F16.opExtrude","CAP_FACE",FACE,{"disambiguationData":[OSD([subQ68,subQ67,sQuery(id+"F8.wireOp",EDGE,"E87"),subQ66])],"isStart":true});var subQ70=sQuery(id+"F8.wireOp",EDGE,"E144");var subQ71=sQuery(id+"F8.wireOp",EDGE,"E143");var subQ72=sQuery(id+"F8.wireOp",EDGE,"E142");var subQ73=sQuery(id+"F8.wireOp",EDGE,"E137");var subQ74=sQuery(id+"F8.wireOp",EDGE,"E136");var subQ75=sQuery(id+"F8.wireOp",EDGE,"E135");var subQ76=sQuery(id+"F8.wireOp",EDGE,"E134");var subQ77=sQuery(id+"F8.wireOp",EDGE,"E133");var subQ78=sQuery(id+"F8.wireOp",EDGE,"E132");var subQ79=sQuery(id+"F8.wireOp",EDGE,"E124");var subQ80=sQuery(id+"F8.wireOp",EDGE,"E122");var subQ81=sQuery(id+"F8.wireOp",EDGE,"E119");var subQ82=sQuery(id+"F8.wireOp",EDGE,"E118");var subQ83=sQuery(id+"F8.wireOp",EDGE,"E116");var subQ84=sQuery(id+"F8.wireOp",EDGE,"E114");var subQ85=sQuery(id+"F8.wireOp",EDGE,"E112");var subQ86=sQuery(id+"F8.wireOp",EDGE,"E110");var subQ87=sQuery(id+"F8.wireOp",EDGE,"E108");var subQ88=sQuery(id+"F8.wireOp",EDGE,"E106");var subQ89=sQuery(id+"F8.wireOp",EDGE,"E104");var subQ90=sQuery(id+"F8.wireOp",EDGE,"E102");var subQ91=sQuery(id+"F8.wireOp",EDGE,"E100");var subQ92=sQuery(id+"F8.wireOp",EDGE,"E98");var subQ93=sQuery(id+"F8.wireOp",EDGE,"E96");var subQ94=sQuery(id+"F8.wireOp",EDGE,"E94");var subQ95=sQuery(id+"F8.wireOp",EDGE,"E92");var subQ96=sQuery(id+"F8.wireOp",EDGE,"E90");var subQ97=sQuery(id+"F8.wireOp",EDGE,"E88");var subQ98=sQuery(id+"F8.wireOp",EDGE,"E86");var subQ99=sQuery(id+"F8.wireOp",EDGE,"E84");var subQ100=sQuery(id+"F8.wireOp",EDGE,"E82");var subQ101=sQuery(id+"F8.wireOp",EDGE,"E80");var subQ102=sQuery(id+"F8.wireOp",EDGE,"E78");var subQ103=sQuery(id+"F8.wireOp",EDGE,"E76");var subQ104=sQuery(id+"F8.wireOp",EDGE,"E72.MirrorCS");var subQ105=sQuery(id+"F8.wireOp",EDGE,"E71.MirrorCS");var subQ106=sQuery(id+"F8.wireOp",EDGE,"E70.MirrorCS");var subQ107=sQuery(id+"F8.wireOp",EDGE,"E67.MirrorCS");var subQ108=sQuery(id+"F8.wireOp",EDGE,"E59.MirrorCS");var subQ109=sQuery(id+"F8.wireOp",EDGE,"E58.MirrorCS");var subQ110=sQuery(id+"F8.wireOp",EDGE,"E57");var subQ111=sQuery(id+"F8.wireOp",EDGE,"E56");var subQ112=sQuery(id+"F8.wireOp",EDGE,"E55");var subQ113=sQuery(id+"F8.wireOp",EDGE,"E54");var subQ114=sQuery(id+"F8.wireOp",EDGE,"E50");var subQ115=sQuery(id+"F8.wireOp",EDGE,"E49");var subQ116=sQuery(id+"F8.wireOp",EDGE,"E48.MirrorCS");var subQ117=sQuery(id+"F8.wireOp",EDGE,"E47.MirrorCS");var subQ118=sQuery(id+"F8.wireOp",EDGE,"E34.MirrorCS");var subQ119=sQuery(id+"F8.wireOp",EDGE,"E33");var subQ120=sQuery(id+"F8.wireOp",EDGE,"E32");var subQ121=sQuery(id+"F8.wireOp",EDGE,"E31");var subQ122=sQuery(id+"F8.wireOp",EDGE,"E30");var subQ123=sQuery(id+"F8.wireOp",EDGE,"E29");var subQ124=sQuery(id+"F8.wireOp",EDGE,"E1.0");var subQ125=makeQuery(id+"F15.opExtrude","CAP_FACE",FACE,{"disambiguationData":[OSD([subQ124,subQ68,subQ63,subQ123,subQ122,subQ121,subQ120,subQ119,subQ118,subQ59,subQ55,subQ51,subQ47,subQ43,subQ39,subQ35,subQ31,subQ27,subQ18,subQ13,subQ2,subQ117,subQ116,subQ115,subQ114,subQ42,subQ67,subQ62,subQ113,subQ112,subQ111,subQ110,subQ109,subQ108,subQ58,subQ54,subQ50,subQ38,subQ34,subQ30,subQ26,subQ107,subQ12,subQ1,subQ106,subQ105,subQ104,subQ46,subQ17,subQ103,subQ102,subQ101,subQ100,subQ99,subQ98,subQ97,subQ96,subQ95,subQ94,subQ93,subQ92,subQ91,subQ90,subQ89,subQ88,subQ87,subQ86,subQ85,subQ84,subQ83,subQ82,subQ81,subQ80,subQ79,subQ25,subQ29,subQ33,subQ37,subQ41,subQ66,subQ61,subQ78,subQ77,subQ76,subQ75,subQ74,subQ73,subQ57,subQ53,subQ49,subQ45,subQ72,subQ71,subQ70,subQ0,subQ11,subQ16])],"isStart":true});var subQ126=makeQuery(id+"F16.opExtrude","CAP_FACE",FACE,{"disambiguationData":[OSD([subQ114,subQ107,sQuery(id+"F8.wireOp",EDGE,"E123"),subQ79])],"isStart":true});var subQ127=makeQuery(id+"F16.opExtrude","CAP_FACE",FACE,{"disambiguationData":[OSD([subQ119,subQ109,sQuery(id+"F8.wireOp",EDGE,"E99"),subQ74])],"isStart":true});var subQ129=makeQuery(id+"F16.opExtrude","CAP_FACE",FACE,{"disambiguationData":[OSD([subQ123,subQ113,sQuery(id+"F8.wireOp",EDGE,"E91"),subQ78])],"isStart":true});var subQ130=makeQuery(id+"F16.opExtrude","CAP_FACE",FACE,{"disambiguationData":[OSD([subQ122,subQ112,sQuery(id+"F8.wireOp",EDGE,"E93"),subQ77])],"isStart":true});var subQ131=makeQuery(id+"F19.opExtrude","CAP_FACE",FACE,{"disambiguationData":[OSD([subQ9,subQ8,subQ7,subQ6,subQ5,subQ4])],"isStart":true});var subQ132=makeQuery(id+"F16.opExtrude","CAP_FACE",FACE,{"disambiguationData":[OSD([subQ121,subQ111,sQuery(id+"F8.wireOp",EDGE,"E95"),subQ76])],"isStart":true});var subQ133=makeQuery(id+"F19.opExtrude","SWEPT_FACE",FACE,{"disambiguationData":[OSD([subQ7])]});var subQ139=makeQuery(id+"F15.opExtrude","CAP_FACE",FACE,{"disambiguationData":[OSD([subQ124,subQ68,subQ63,subQ123,subQ122,subQ121,subQ120,subQ119,subQ118,subQ59,subQ55,subQ51,subQ47,subQ43,subQ39,subQ35,subQ31,subQ27,subQ18,subQ13,subQ2,subQ117,subQ116,subQ115,subQ114,subQ42,subQ67,subQ62,subQ113,subQ112,subQ111,subQ110,subQ109,subQ108,subQ58,subQ54,subQ50,subQ38,subQ34,subQ30,subQ26,subQ107,subQ12,subQ1,subQ106,subQ105,subQ104,subQ46,subQ17,subQ103,subQ102,subQ101,subQ100,subQ99,subQ98,subQ97,subQ96,subQ95,subQ94,subQ93,subQ92,subQ91,subQ90,subQ89,subQ88,subQ87,subQ86,subQ85,subQ84,subQ83,subQ82,subQ81,subQ80,subQ79,subQ25,subQ29,subQ33,subQ37,subQ41,subQ66,subQ61,subQ78,subQ77,subQ76,subQ75,subQ74,subQ73,subQ57,subQ53,subQ49,subQ45,subQ72,subQ71,subQ70,subQ0,subQ11,subQ16])],"isStart":false});var subQ140=makeQuery(id+"F16.opExtrude","CAP_FACE",FACE,{"disambiguationData":[OSD([subQ120,subQ110,sQuery(id+"F8.wireOp",EDGE,"E97"),subQ75])],"isStart":true});var subQ141=makeQuery(id+"F19.opExtrude","SWEPT_FACE",FACE,{"disambiguationData":[OSD([subQ4])]});var subQ142=makeQuery(id+"F16.opExtrude","CAP_FACE",FACE,{"disambiguationData":[OSD([subQ118,subQ108,sQuery(id+"F8.wireOp",EDGE,"E101"),subQ73])],"isStart":true});var subQ143=makeQuery(id+"F16.opExtrude","CAP_FACE",FACE,{"disambiguationData":[OSD([subQ117,subQ106,sQuery(id+"F8.wireOp",EDGE,"E115"),subQ70])],"isStart":true});var subQ144=makeQuery(id+"F16.opExtrude","CAP_FACE",FACE,{"disambiguationData":[OSD([subQ116,subQ105,sQuery(id+"F8.wireOp",EDGE,"E113"),subQ71])],"isStart":true});var subQ145=makeQuery(id+"F16.opExtrude","CAP_FACE",FACE,{"disambiguationData":[OSD([subQ115,subQ104,sQuery(id+"F8.wireOp",EDGE,"E111"),subQ72])],"isStart":true});var subQ146=makeQuery(id+"F18.opRevolve","SWEPT_FACE",FACE,{"disambiguationData":[OSD([subQ20])]});var subQ147=makeQuery(id+"F19.opExtrude","SWEPT_FACE",FACE,{"disambiguationData":[OSD([subQ8])]});var subQ148=makeQuery(id+"F19.opExtrude","SWEPT_FACE",FACE,{"disambiguationData":[OSD([subQ5])]});Q0=makeQuery(id+"F21.boolean.opBoolean","INTERSECT",EDGE,{"derivedFrom":[makeQuery(id+"F20.boolean.opBoolean","SPLIT",FACE,{"disambiguationData":[TD([subQ15])],"derivedFrom":makeQuery(id+"F19.boolean.opBoolean","SPLIT",FACE,{"disambiguationData":[TD([makeQuery(id+"F15.opExtrude","SWEPT_FACE",FACE,{"disambiguationData":[OSD([subQ124])]}),subQ125,subQ139,subQ69,subQ64,subQ129,subQ130,subQ132,subQ140,subQ127,subQ142,subQ60,subQ56,subQ52,subQ48,subQ44,subQ40,subQ36,subQ32,subQ28,subQ19,subQ14,subQ3,subQ143,subQ144,subQ145,subQ126,subQ65,subQ24,subQ15,subQ146,subQ131,subQ10,subQ147,subQ133,subQ148,subQ141])],"derivedFrom":makeQuery(id+"F18.boolean.opBoolean","MERGE",FACE,{"derivedFrom":[makeQuery(id+"F17.opRevolve","SWEPT_FACE",FACE,{"disambiguationData":[OSD([subQ23])]}),makeQuery(id+"F18.opRevolve","SWEPT_FACE",FACE,{"disambiguationData":[OSD([subQ23])]})]})})}),makeQuery(id+"F21.opExtrude","SWEPT_FACE",FACE,{"disambiguationData":[OSD([sQuery(id+"F13.wireOp",EDGE,"E296.MirrorCS")])]})]});}
            var Q1;
            {var subQ0=sQuery(id+"F8.wireOp",EDGE,"E145");var subQ1=sQuery(id+"F8.wireOp",EDGE,"E69.MirrorCS");var subQ2=sQuery(id+"F8.wireOp",EDGE,"E46.MirrorCS");var subQ3=makeQuery(id+"F16.opExtrude","CAP_FACE",FACE,{"disambiguationData":[OSD([subQ2,subQ1,sQuery(id+"F8.wireOp",EDGE,"E117"),subQ0])],"isStart":true});var subQ4=sQuery(id+"F12.wireOp",EDGE,"E290");var subQ5=sQuery(id+"F12.wireOp",EDGE,"E289");var subQ6=sQuery(id+"F12.wireOp",EDGE,"E288");var subQ7=sQuery(id+"F12.wireOp",EDGE,"E287");var subQ8=sQuery(id+"F12.wireOp",EDGE,"E286");var subQ9=sQuery(id+"F12.wireOp",EDGE,"E285");var subQ10=makeQuery(id+"F19.opExtrude","CAP_FACE",FACE,{"disambiguationData":[OSD([subQ9,subQ8,subQ7,subQ6,subQ5,subQ4])],"isStart":false});var subQ11=sQuery(id+"F8.wireOp",EDGE,"E146");var subQ12=sQuery(id+"F8.wireOp",EDGE,"E68.MirrorCS");var subQ13=sQuery(id+"F8.wireOp",EDGE,"E45.MirrorCS");var subQ14=makeQuery(id+"F16.opExtrude","CAP_FACE",FACE,{"disambiguationData":[OSD([subQ13,subQ12,sQuery(id+"F8.wireOp",EDGE,"E120"),subQ11])],"isStart":true});var subQ15=makeQuery(id+"F18.opRevolve","SWEPT_FACE",FACE,{"disambiguationData":[OSD([sQuery(id+"F9.wireOp",EDGE,"E157")])]});var subQ16=sQuery(id+"F8.wireOp",EDGE,"E147");var subQ17=sQuery(id+"F8.wireOp",EDGE,"E74");var subQ18=sQuery(id+"F8.wireOp",EDGE,"E44.MirrorCS");var subQ19=makeQuery(id+"F16.opExtrude","CAP_FACE",FACE,{"disambiguationData":[OSD([subQ18,subQ17,sQuery(id+"F8.wireOp",EDGE,"E121"),subQ16])],"isStart":true});var subQ20=sQuery(id+"F9.wireOp",EDGE,"E164");var subQ21=sQuery(id+"F9.wireOp",EDGE,"E152");var subQ22=sQuery(id+"F9.wireOp",EDGE,"E151");var subQ23=sQuery(id+"F9.wireOp",EDGE,"E150");var subQ24=makeQuery(id+"F17.opRevolve","CAP_FACE",FACE,{"disambiguationData":[OSD([subQ23,subQ22,subQ21,subQ20])],"isStart":false});var subQ25=sQuery(id+"F8.wireOp",EDGE,"E125");var subQ26=sQuery(id+"F8.wireOp",EDGE,"E66.MirrorCS");var subQ27=sQuery(id+"F8.wireOp",EDGE,"E43.MirrorCS");var subQ28=makeQuery(id+"F16.opExtrude","CAP_FACE",FACE,{"disambiguationData":[OSD([subQ27,subQ26,sQuery(id+"F8.wireOp",EDGE,"E77"),subQ25])],"isStart":true});var subQ29=sQuery(id+"F8.wireOp",EDGE,"E126");var subQ30=sQuery(id+"F8.wireOp",EDGE,"E65.MirrorCS");var subQ31=sQuery(id+"F8.wireOp",EDGE,"E42.MirrorCS");var subQ32=makeQuery(id+"F16.opExtrude","CAP_FACE",FACE,{"disambiguationData":[OSD([subQ31,subQ30,sQuery(id+"F8.wireOp",EDGE,"E79"),subQ29])],"isStart":true});var subQ33=sQuery(id+"F8.wireOp",EDGE,"E127");var subQ34=sQuery(id+"F8.wireOp",EDGE,"E64.MirrorCS");var subQ35=sQuery(id+"F8.wireOp",EDGE,"E41.MirrorCS");var subQ36=makeQuery(id+"F16.opExtrude","CAP_FACE",FACE,{"disambiguationData":[OSD([subQ35,subQ34,sQuery(id+"F8.wireOp",EDGE,"E81"),subQ33])],"isStart":true});var subQ37=sQuery(id+"F8.wireOp",EDGE,"E128");var subQ38=sQuery(id+"F8.wireOp",EDGE,"E63.MirrorCS");var subQ39=sQuery(id+"F8.wireOp",EDGE,"E40.MirrorCS");var subQ40=makeQuery(id+"F16.opExtrude","CAP_FACE",FACE,{"disambiguationData":[OSD([subQ39,subQ38,sQuery(id+"F8.wireOp",EDGE,"E83"),subQ37])],"isStart":true});var subQ41=sQuery(id+"F8.wireOp",EDGE,"E129");var subQ42=sQuery(id+"F8.wireOp",EDGE,"E51");var subQ43=sQuery(id+"F8.wireOp",EDGE,"E39.MirrorCS");var subQ44=makeQuery(id+"F16.opExtrude","CAP_FACE",FACE,{"disambiguationData":[OSD([subQ43,subQ42,sQuery(id+"F8.wireOp",EDGE,"E85"),subQ41])],"isStart":true});var subQ45=sQuery(id+"F8.wireOp",EDGE,"E141");var subQ46=sQuery(id+"F8.wireOp",EDGE,"E73");var subQ47=sQuery(id+"F8.wireOp",EDGE,"E38.MirrorCS");var subQ48=makeQuery(id+"F16.opExtrude","CAP_FACE",FACE,{"disambiguationData":[OSD([subQ47,subQ46,sQuery(id+"F8.wireOp",EDGE,"E109"),subQ45])],"isStart":true});var subQ49=sQuery(id+"F8.wireOp",EDGE,"E140");var subQ50=sQuery(id+"F8.wireOp",EDGE,"E62.MirrorCS");var subQ51=sQuery(id+"F8.wireOp",EDGE,"E37.MirrorCS");var subQ52=makeQuery(id+"F16.opExtrude","CAP_FACE",FACE,{"disambiguationData":[OSD([subQ51,subQ50,sQuery(id+"F8.wireOp",EDGE,"E107"),subQ49])],"isStart":true});var subQ53=sQuery(id+"F8.wireOp",EDGE,"E139");var subQ54=sQuery(id+"F8.wireOp",EDGE,"E61.MirrorCS");var subQ55=sQuery(id+"F8.wireOp",EDGE,"E36.MirrorCS");var subQ56=makeQuery(id+"F16.opExtrude","CAP_FACE",FACE,{"disambiguationData":[OSD([subQ55,subQ54,sQuery(id+"F8.wireOp",EDGE,"E105"),subQ53])],"isStart":true});var subQ57=sQuery(id+"F8.wireOp",EDGE,"E138");var subQ58=sQuery(id+"F8.wireOp",EDGE,"E60.MirrorCS");var subQ59=sQuery(id+"F8.wireOp",EDGE,"E35.MirrorCS");var subQ60=makeQuery(id+"F16.opExtrude","CAP_FACE",FACE,{"disambiguationData":[OSD([subQ59,subQ58,sQuery(id+"F8.wireOp",EDGE,"E103"),subQ57])],"isStart":true});var subQ61=sQuery(id+"F8.wireOp",EDGE,"E131");var subQ62=sQuery(id+"F8.wireOp",EDGE,"E53");var subQ63=sQuery(id+"F8.wireOp",EDGE,"E28");var subQ64=makeQuery(id+"F16.opExtrude","CAP_FACE",FACE,{"disambiguationData":[OSD([subQ63,subQ62,sQuery(id+"F8.wireOp",EDGE,"E89"),subQ61])],"isStart":true});var subQ65=makeQuery(id+"F17.opRevolve","CAP_FACE",FACE,{"disambiguationData":[OSD([subQ23,subQ22,subQ21,subQ20])],"isStart":true});var subQ66=sQuery(id+"F8.wireOp",EDGE,"E130");var subQ67=sQuery(id+"F8.wireOp",EDGE,"E52");var subQ68=sQuery(id+"F8.wireOp",EDGE,"E27");var subQ69=makeQuery(id+"F16.opExtrude","CAP_FACE",FACE,{"disambiguationData":[OSD([subQ68,subQ67,sQuery(id+"F8.wireOp",EDGE,"E87"),subQ66])],"isStart":true});var subQ70=sQuery(id+"F8.wireOp",EDGE,"E144");var subQ71=sQuery(id+"F8.wireOp",EDGE,"E143");var subQ72=sQuery(id+"F8.wireOp",EDGE,"E142");var subQ73=sQuery(id+"F8.wireOp",EDGE,"E137");var subQ74=sQuery(id+"F8.wireOp",EDGE,"E136");var subQ75=sQuery(id+"F8.wireOp",EDGE,"E135");var subQ76=sQuery(id+"F8.wireOp",EDGE,"E134");var subQ77=sQuery(id+"F8.wireOp",EDGE,"E133");var subQ78=sQuery(id+"F8.wireOp",EDGE,"E132");var subQ79=sQuery(id+"F8.wireOp",EDGE,"E124");var subQ80=sQuery(id+"F8.wireOp",EDGE,"E122");var subQ81=sQuery(id+"F8.wireOp",EDGE,"E119");var subQ82=sQuery(id+"F8.wireOp",EDGE,"E118");var subQ83=sQuery(id+"F8.wireOp",EDGE,"E116");var subQ84=sQuery(id+"F8.wireOp",EDGE,"E114");var subQ85=sQuery(id+"F8.wireOp",EDGE,"E112");var subQ86=sQuery(id+"F8.wireOp",EDGE,"E110");var subQ87=sQuery(id+"F8.wireOp",EDGE,"E108");var subQ88=sQuery(id+"F8.wireOp",EDGE,"E106");var subQ89=sQuery(id+"F8.wireOp",EDGE,"E104");var subQ90=sQuery(id+"F8.wireOp",EDGE,"E102");var subQ91=sQuery(id+"F8.wireOp",EDGE,"E100");var subQ92=sQuery(id+"F8.wireOp",EDGE,"E98");var subQ93=sQuery(id+"F8.wireOp",EDGE,"E96");var subQ94=sQuery(id+"F8.wireOp",EDGE,"E94");var subQ95=sQuery(id+"F8.wireOp",EDGE,"E92");var subQ96=sQuery(id+"F8.wireOp",EDGE,"E90");var subQ97=sQuery(id+"F8.wireOp",EDGE,"E88");var subQ98=sQuery(id+"F8.wireOp",EDGE,"E86");var subQ99=sQuery(id+"F8.wireOp",EDGE,"E84");var subQ100=sQuery(id+"F8.wireOp",EDGE,"E82");var subQ101=sQuery(id+"F8.wireOp",EDGE,"E80");var subQ102=sQuery(id+"F8.wireOp",EDGE,"E78");var subQ103=sQuery(id+"F8.wireOp",EDGE,"E76");var subQ104=sQuery(id+"F8.wireOp",EDGE,"E72.MirrorCS");var subQ105=sQuery(id+"F8.wireOp",EDGE,"E71.MirrorCS");var subQ106=sQuery(id+"F8.wireOp",EDGE,"E70.MirrorCS");var subQ107=sQuery(id+"F8.wireOp",EDGE,"E67.MirrorCS");var subQ108=sQuery(id+"F8.wireOp",EDGE,"E59.MirrorCS");var subQ109=sQuery(id+"F8.wireOp",EDGE,"E58.MirrorCS");var subQ110=sQuery(id+"F8.wireOp",EDGE,"E57");var subQ111=sQuery(id+"F8.wireOp",EDGE,"E56");var subQ112=sQuery(id+"F8.wireOp",EDGE,"E55");var subQ113=sQuery(id+"F8.wireOp",EDGE,"E54");var subQ114=sQuery(id+"F8.wireOp",EDGE,"E50");var subQ115=sQuery(id+"F8.wireOp",EDGE,"E49");var subQ116=sQuery(id+"F8.wireOp",EDGE,"E48.MirrorCS");var subQ117=sQuery(id+"F8.wireOp",EDGE,"E47.MirrorCS");var subQ118=sQuery(id+"F8.wireOp",EDGE,"E34.MirrorCS");var subQ119=sQuery(id+"F8.wireOp",EDGE,"E33");var subQ120=sQuery(id+"F8.wireOp",EDGE,"E32");var subQ121=sQuery(id+"F8.wireOp",EDGE,"E31");var subQ122=sQuery(id+"F8.wireOp",EDGE,"E30");var subQ123=sQuery(id+"F8.wireOp",EDGE,"E29");var subQ124=sQuery(id+"F8.wireOp",EDGE,"E1.0");var subQ125=makeQuery(id+"F15.opExtrude","CAP_FACE",FACE,{"disambiguationData":[OSD([subQ124,subQ68,subQ63,subQ123,subQ122,subQ121,subQ120,subQ119,subQ118,subQ59,subQ55,subQ51,subQ47,subQ43,subQ39,subQ35,subQ31,subQ27,subQ18,subQ13,subQ2,subQ117,subQ116,subQ115,subQ114,subQ42,subQ67,subQ62,subQ113,subQ112,subQ111,subQ110,subQ109,subQ108,subQ58,subQ54,subQ50,subQ38,subQ34,subQ30,subQ26,subQ107,subQ12,subQ1,subQ106,subQ105,subQ104,subQ46,subQ17,subQ103,subQ102,subQ101,subQ100,subQ99,subQ98,subQ97,subQ96,subQ95,subQ94,subQ93,subQ92,subQ91,subQ90,subQ89,subQ88,subQ87,subQ86,subQ85,subQ84,subQ83,subQ82,subQ81,subQ80,subQ79,subQ25,subQ29,subQ33,subQ37,subQ41,subQ66,subQ61,subQ78,subQ77,subQ76,subQ75,subQ74,subQ73,subQ57,subQ53,subQ49,subQ45,subQ72,subQ71,subQ70,subQ0,subQ11,subQ16])],"isStart":true});var subQ126=makeQuery(id+"F16.opExtrude","CAP_FACE",FACE,{"disambiguationData":[OSD([subQ114,subQ107,sQuery(id+"F8.wireOp",EDGE,"E123"),subQ79])],"isStart":true});var subQ127=makeQuery(id+"F16.opExtrude","CAP_FACE",FACE,{"disambiguationData":[OSD([subQ119,subQ109,sQuery(id+"F8.wireOp",EDGE,"E99"),subQ74])],"isStart":true});var subQ129=makeQuery(id+"F16.opExtrude","CAP_FACE",FACE,{"disambiguationData":[OSD([subQ123,subQ113,sQuery(id+"F8.wireOp",EDGE,"E91"),subQ78])],"isStart":true});var subQ130=makeQuery(id+"F16.opExtrude","CAP_FACE",FACE,{"disambiguationData":[OSD([subQ122,subQ112,sQuery(id+"F8.wireOp",EDGE,"E93"),subQ77])],"isStart":true});var subQ131=makeQuery(id+"F19.opExtrude","CAP_FACE",FACE,{"disambiguationData":[OSD([subQ9,subQ8,subQ7,subQ6,subQ5,subQ4])],"isStart":true});var subQ132=makeQuery(id+"F16.opExtrude","CAP_FACE",FACE,{"disambiguationData":[OSD([subQ121,subQ111,sQuery(id+"F8.wireOp",EDGE,"E95"),subQ76])],"isStart":true});var subQ133=makeQuery(id+"F19.opExtrude","SWEPT_FACE",FACE,{"disambiguationData":[OSD([subQ7])]});var subQ139=makeQuery(id+"F15.opExtrude","CAP_FACE",FACE,{"disambiguationData":[OSD([subQ124,subQ68,subQ63,subQ123,subQ122,subQ121,subQ120,subQ119,subQ118,subQ59,subQ55,subQ51,subQ47,subQ43,subQ39,subQ35,subQ31,subQ27,subQ18,subQ13,subQ2,subQ117,subQ116,subQ115,subQ114,subQ42,subQ67,subQ62,subQ113,subQ112,subQ111,subQ110,subQ109,subQ108,subQ58,subQ54,subQ50,subQ38,subQ34,subQ30,subQ26,subQ107,subQ12,subQ1,subQ106,subQ105,subQ104,subQ46,subQ17,subQ103,subQ102,subQ101,subQ100,subQ99,subQ98,subQ97,subQ96,subQ95,subQ94,subQ93,subQ92,subQ91,subQ90,subQ89,subQ88,subQ87,subQ86,subQ85,subQ84,subQ83,subQ82,subQ81,subQ80,subQ79,subQ25,subQ29,subQ33,subQ37,subQ41,subQ66,subQ61,subQ78,subQ77,subQ76,subQ75,subQ74,subQ73,subQ57,subQ53,subQ49,subQ45,subQ72,subQ71,subQ70,subQ0,subQ11,subQ16])],"isStart":false});var subQ140=makeQuery(id+"F16.opExtrude","CAP_FACE",FACE,{"disambiguationData":[OSD([subQ120,subQ110,sQuery(id+"F8.wireOp",EDGE,"E97"),subQ75])],"isStart":true});var subQ141=makeQuery(id+"F19.opExtrude","SWEPT_FACE",FACE,{"disambiguationData":[OSD([subQ4])]});var subQ142=makeQuery(id+"F16.opExtrude","CAP_FACE",FACE,{"disambiguationData":[OSD([subQ118,subQ108,sQuery(id+"F8.wireOp",EDGE,"E101"),subQ73])],"isStart":true});var subQ143=makeQuery(id+"F16.opExtrude","CAP_FACE",FACE,{"disambiguationData":[OSD([subQ117,subQ106,sQuery(id+"F8.wireOp",EDGE,"E115"),subQ70])],"isStart":true});var subQ144=makeQuery(id+"F16.opExtrude","CAP_FACE",FACE,{"disambiguationData":[OSD([subQ116,subQ105,sQuery(id+"F8.wireOp",EDGE,"E113"),subQ71])],"isStart":true});var subQ145=makeQuery(id+"F16.opExtrude","CAP_FACE",FACE,{"disambiguationData":[OSD([subQ115,subQ104,sQuery(id+"F8.wireOp",EDGE,"E111"),subQ72])],"isStart":true});var subQ146=makeQuery(id+"F18.opRevolve","SWEPT_FACE",FACE,{"disambiguationData":[OSD([subQ20])]});var subQ147=makeQuery(id+"F19.opExtrude","SWEPT_FACE",FACE,{"disambiguationData":[OSD([subQ8])]});var subQ148=makeQuery(id+"F19.opExtrude","SWEPT_FACE",FACE,{"disambiguationData":[OSD([subQ5])]});Q1=makeQuery(id+"F21.boolean.opBoolean","INTERSECT",EDGE,{"derivedFrom":[makeQuery(id+"F20.boolean.opBoolean","SPLIT",FACE,{"disambiguationData":[TD([subQ15])],"derivedFrom":makeQuery(id+"F19.boolean.opBoolean","SPLIT",FACE,{"disambiguationData":[TD([makeQuery(id+"F15.opExtrude","SWEPT_FACE",FACE,{"disambiguationData":[OSD([subQ124])]}),subQ125,subQ139,subQ69,subQ64,subQ129,subQ130,subQ132,subQ140,subQ127,subQ142,subQ60,subQ56,subQ52,subQ48,subQ44,subQ40,subQ36,subQ32,subQ28,subQ19,subQ14,subQ3,subQ143,subQ144,subQ145,subQ126,subQ65,subQ24,subQ15,subQ146,subQ131,subQ10,subQ147,subQ133,subQ148,subQ141])],"derivedFrom":makeQuery(id+"F18.boolean.opBoolean","MERGE",FACE,{"derivedFrom":[makeQuery(id+"F17.opRevolve","SWEPT_FACE",FACE,{"disambiguationData":[OSD([subQ23])]}),makeQuery(id+"F18.opRevolve","SWEPT_FACE",FACE,{"disambiguationData":[OSD([subQ23])]})]})})}),makeQuery(id+"F21.opExtrude","SWEPT_FACE",FACE,{"disambiguationData":[OSD([sQuery(id+"F13.wireOp",EDGE,"E295.MirrorCS")])]})]});}
            fillet(context, id + "F38", {"entities" : qUnion([Q0, Q1]), "radius" : 5 * mm, "tangentPropagation" : true, "allowEdgeOverflow" : false});
        }
        {
            var Q0;
            Q0=makeQuery(id+"F24.boolean.opBoolean","MERGE",EDGE,{"derivedFrom":[makeQuery(id+"F23.opExtrude","SWEPT_EDGE",EDGE,{"disambiguationData":[OSD([sQuery(id+"F13.wireOp",EDGE,"E307"),sQuery(id+"F13.wireOp",EDGE,"E308")])]}),makeQuery(id+"F24.opExtrude","SWEPT_EDGE",EDGE,{"disambiguationData":[OSD([sQuery(id+"F14.wireOp",EDGE,"E325"),sQuery(id+"F14.wireOp",EDGE,"E326")])]})]});
            var Q1;
            Q1=makeQuery(id+"F24.boolean.opBoolean","MERGE",EDGE,{"derivedFrom":[makeQuery(id+"F23.opExtrude","SWEPT_EDGE",EDGE,{"disambiguationData":[OSD([sQuery(id+"F13.wireOp",EDGE,"E308"),sQuery(id+"F13.wireOp",EDGE,"E309")])]}),makeQuery(id+"F24.opExtrude","SWEPT_EDGE",EDGE,{"disambiguationData":[OSD([sQuery(id+"F14.wireOp",EDGE,"E326"),sQuery(id+"F14.wireOp",EDGE,"E327")])]})]});
            var Q2;
            Q2=makeQuery(id+"F24.opExtrude","SWEPT_EDGE",EDGE,{"disambiguationData":[OSD([sQuery(id+"F14.wireOp",EDGE,"E314.MirrorCS"),sQuery(id+"F14.wireOp",EDGE,"E329.0")])]});
            var Q3;
            Q3=makeQuery(id+"F24.opExtrude","SWEPT_EDGE",EDGE,{"disambiguationData":[OSD([sQuery(id+"F14.wireOp",EDGE,"E313.MirrorCS"),sQuery(id+"F14.wireOp",EDGE,"E329.0")])]});
            var Q4;
            Q4=makeQuery(id+"F23.opExtrude","CAP_EDGE",EDGE,{"disambiguationData":[OSD([sQuery(id+"F13.wireOp",EDGE,"E308")])],"isStart":true});
            var Q5;
            Q5=makeQuery(id+"F23.opExtrude","CAP_EDGE",EDGE,{"disambiguationData":[OSD([sQuery(id+"F13.wireOp",EDGE,"E309")])],"isStart":true});
            var Q6;
            Q6=makeQuery(id+"F23.opExtrude","CAP_EDGE",EDGE,{"disambiguationData":[OSD([sQuery(id+"F13.wireOp",EDGE,"E307")])],"isStart":true});
            var Q7;
            {var subQ3=sQuery(id+"F11.wireOp",EDGE,"E261");var subQ4=sQuery(id+"F11.wireOp",EDGE,"E260");var subQ8=sQuery(id+"F9.wireOp",EDGE,"E150");var subQ9=makeQuery(id+"F18.opRevolve","SWEPT_FACE",FACE,{"disambiguationData":[OSD([subQ8])]});var subQ10=makeQuery(id+"F17.opRevolve","SWEPT_FACE",FACE,{"disambiguationData":[OSD([subQ8])]});var subQ11=makeQuery(id+"F20.opExtrude","SWEPT_FACE",FACE,{"disambiguationData":[OSD([subQ4])]});var subQ12=makeQuery(id+"F21.opExtrude","SWEPT_FACE",FACE,{"disambiguationData":[OSD([sQuery(id+"F13.wireOp",EDGE,"E296.MirrorCS")])]});var subQ13=sQuery(id+"F13.wireOp",EDGE,"E309");var subQ14=makeQuery(id+"F20.opExtrude","SWEPT_FACE",FACE,{"disambiguationData":[OSD([subQ3])]});var subQ15=sQuery(id+"F12.wireOp",EDGE,"E287");var subQ16=makeQuery(id+"F19.opExtrude","SWEPT_FACE",FACE,{"disambiguationData":[OSD([subQ15])]});var subQ17=sQuery(id+"F8.wireOp",EDGE,"E145");var subQ18=sQuery(id+"F8.wireOp",EDGE,"E69.MirrorCS");var subQ19=sQuery(id+"F8.wireOp",EDGE,"E46.MirrorCS");var subQ20=makeQuery(id+"F16.opExtrude","CAP_FACE",FACE,{"disambiguationData":[OSD([subQ19,subQ18,sQuery(id+"F8.wireOp",EDGE,"E117"),subQ17])],"isStart":true});var subQ21=sQuery(id+"F12.wireOp",EDGE,"E290");var subQ22=sQuery(id+"F12.wireOp",EDGE,"E289");var subQ23=sQuery(id+"F12.wireOp",EDGE,"E288");var subQ24=sQuery(id+"F12.wireOp",EDGE,"E286");var subQ25=sQuery(id+"F12.wireOp",EDGE,"E285");var subQ26=makeQuery(id+"F19.opExtrude","CAP_FACE",FACE,{"disambiguationData":[OSD([subQ25,subQ24,subQ15,subQ23,subQ22,subQ21])],"isStart":false});var subQ27=sQuery(id+"F8.wireOp",EDGE,"E146");var subQ28=sQuery(id+"F8.wireOp",EDGE,"E68.MirrorCS");var subQ29=sQuery(id+"F8.wireOp",EDGE,"E45.MirrorCS");var subQ30=makeQuery(id+"F16.opExtrude","CAP_FACE",FACE,{"disambiguationData":[OSD([subQ29,subQ28,sQuery(id+"F8.wireOp",EDGE,"E120"),subQ27])],"isStart":true});var subQ31=makeQuery(id+"F18.opRevolve","SWEPT_FACE",FACE,{"disambiguationData":[OSD([sQuery(id+"F9.wireOp",EDGE,"E157")])]});var subQ32=sQuery(id+"F8.wireOp",EDGE,"E147");var subQ33=sQuery(id+"F8.wireOp",EDGE,"E74");var subQ34=sQuery(id+"F8.wireOp",EDGE,"E44.MirrorCS");var subQ35=makeQuery(id+"F16.opExtrude","CAP_FACE",FACE,{"disambiguationData":[OSD([subQ34,subQ33,sQuery(id+"F8.wireOp",EDGE,"E121"),subQ32])],"isStart":true});var subQ36=sQuery(id+"F9.wireOp",EDGE,"E164");var subQ37=sQuery(id+"F9.wireOp",EDGE,"E152");var subQ38=sQuery(id+"F9.wireOp",EDGE,"E151");var subQ39=makeQuery(id+"F17.opRevolve","CAP_FACE",FACE,{"disambiguationData":[OSD([subQ8,subQ38,subQ37,subQ36])],"isStart":false});var subQ40=sQuery(id+"F8.wireOp",EDGE,"E125");var subQ41=sQuery(id+"F8.wireOp",EDGE,"E66.MirrorCS");var subQ42=sQuery(id+"F8.wireOp",EDGE,"E43.MirrorCS");var subQ43=makeQuery(id+"F16.opExtrude","CAP_FACE",FACE,{"disambiguationData":[OSD([subQ42,subQ41,sQuery(id+"F8.wireOp",EDGE,"E77"),subQ40])],"isStart":true});var subQ44=sQuery(id+"F8.wireOp",EDGE,"E126");var subQ45=sQuery(id+"F8.wireOp",EDGE,"E65.MirrorCS");var subQ46=sQuery(id+"F8.wireOp",EDGE,"E42.MirrorCS");var subQ47=makeQuery(id+"F16.opExtrude","CAP_FACE",FACE,{"disambiguationData":[OSD([subQ46,subQ45,sQuery(id+"F8.wireOp",EDGE,"E79"),subQ44])],"isStart":true});var subQ48=sQuery(id+"F8.wireOp",EDGE,"E127");var subQ49=sQuery(id+"F8.wireOp",EDGE,"E64.MirrorCS");var subQ50=sQuery(id+"F8.wireOp",EDGE,"E41.MirrorCS");var subQ51=makeQuery(id+"F16.opExtrude","CAP_FACE",FACE,{"disambiguationData":[OSD([subQ50,subQ49,sQuery(id+"F8.wireOp",EDGE,"E81"),subQ48])],"isStart":true});var subQ52=sQuery(id+"F8.wireOp",EDGE,"E128");var subQ53=sQuery(id+"F8.wireOp",EDGE,"E63.MirrorCS");var subQ54=sQuery(id+"F8.wireOp",EDGE,"E40.MirrorCS");var subQ55=makeQuery(id+"F16.opExtrude","CAP_FACE",FACE,{"disambiguationData":[OSD([subQ54,subQ53,sQuery(id+"F8.wireOp",EDGE,"E83"),subQ52])],"isStart":true});var subQ56=sQuery(id+"F8.wireOp",EDGE,"E129");var subQ57=sQuery(id+"F8.wireOp",EDGE,"E51");var subQ58=sQuery(id+"F8.wireOp",EDGE,"E39.MirrorCS");var subQ59=makeQuery(id+"F16.opExtrude","CAP_FACE",FACE,{"disambiguationData":[OSD([subQ58,subQ57,sQuery(id+"F8.wireOp",EDGE,"E85"),subQ56])],"isStart":true});var subQ60=sQuery(id+"F8.wireOp",EDGE,"E141");var subQ61=sQuery(id+"F8.wireOp",EDGE,"E73");var subQ62=sQuery(id+"F8.wireOp",EDGE,"E38.MirrorCS");var subQ63=makeQuery(id+"F16.opExtrude","CAP_FACE",FACE,{"disambiguationData":[OSD([subQ62,subQ61,sQuery(id+"F8.wireOp",EDGE,"E109"),subQ60])],"isStart":true});var subQ64=sQuery(id+"F8.wireOp",EDGE,"E140");var subQ65=sQuery(id+"F8.wireOp",EDGE,"E62.MirrorCS");var subQ66=sQuery(id+"F8.wireOp",EDGE,"E37.MirrorCS");var subQ67=makeQuery(id+"F16.opExtrude","CAP_FACE",FACE,{"disambiguationData":[OSD([subQ66,subQ65,sQuery(id+"F8.wireOp",EDGE,"E107"),subQ64])],"isStart":true});var subQ68=sQuery(id+"F8.wireOp",EDGE,"E139");var subQ69=sQuery(id+"F8.wireOp",EDGE,"E61.MirrorCS");var subQ70=sQuery(id+"F8.wireOp",EDGE,"E36.MirrorCS");var subQ71=makeQuery(id+"F16.opExtrude","CAP_FACE",FACE,{"disambiguationData":[OSD([subQ70,subQ69,sQuery(id+"F8.wireOp",EDGE,"E105"),subQ68])],"isStart":true});var subQ72=sQuery(id+"F8.wireOp",EDGE,"E138");var subQ73=sQuery(id+"F8.wireOp",EDGE,"E60.MirrorCS");var subQ74=sQuery(id+"F8.wireOp",EDGE,"E35.MirrorCS");var subQ75=makeQuery(id+"F16.opExtrude","CAP_FACE",FACE,{"disambiguationData":[OSD([subQ74,subQ73,sQuery(id+"F8.wireOp",EDGE,"E103"),subQ72])],"isStart":true});var subQ76=sQuery(id+"F8.wireOp",EDGE,"E131");var subQ77=sQuery(id+"F8.wireOp",EDGE,"E53");var subQ78=sQuery(id+"F8.wireOp",EDGE,"E28");var subQ79=makeQuery(id+"F16.opExtrude","CAP_FACE",FACE,{"disambiguationData":[OSD([subQ78,subQ77,sQuery(id+"F8.wireOp",EDGE,"E89"),subQ76])],"isStart":true});var subQ80=makeQuery(id+"F17.opRevolve","CAP_FACE",FACE,{"disambiguationData":[OSD([subQ8,subQ38,subQ37,subQ36])],"isStart":true});var subQ81=sQuery(id+"F8.wireOp",EDGE,"E130");var subQ82=sQuery(id+"F8.wireOp",EDGE,"E52");var subQ83=sQuery(id+"F8.wireOp",EDGE,"E27");var subQ84=makeQuery(id+"F16.opExtrude","CAP_FACE",FACE,{"disambiguationData":[OSD([subQ83,subQ82,sQuery(id+"F8.wireOp",EDGE,"E87"),subQ81])],"isStart":true});var subQ85=sQuery(id+"F8.wireOp",EDGE,"E144");var subQ86=sQuery(id+"F8.wireOp",EDGE,"E143");var subQ87=sQuery(id+"F8.wireOp",EDGE,"E142");var subQ88=sQuery(id+"F8.wireOp",EDGE,"E137");var subQ89=sQuery(id+"F8.wireOp",EDGE,"E136");var subQ90=sQuery(id+"F8.wireOp",EDGE,"E135");var subQ91=sQuery(id+"F8.wireOp",EDGE,"E134");var subQ92=sQuery(id+"F8.wireOp",EDGE,"E133");var subQ93=sQuery(id+"F8.wireOp",EDGE,"E132");var subQ94=sQuery(id+"F8.wireOp",EDGE,"E124");var subQ95=sQuery(id+"F8.wireOp",EDGE,"E122");var subQ96=sQuery(id+"F8.wireOp",EDGE,"E119");var subQ97=sQuery(id+"F8.wireOp",EDGE,"E118");var subQ98=sQuery(id+"F8.wireOp",EDGE,"E116");var subQ99=sQuery(id+"F8.wireOp",EDGE,"E114");var subQ100=sQuery(id+"F8.wireOp",EDGE,"E112");var subQ101=sQuery(id+"F8.wireOp",EDGE,"E110");var subQ102=sQuery(id+"F8.wireOp",EDGE,"E108");var subQ103=sQuery(id+"F8.wireOp",EDGE,"E106");var subQ104=sQuery(id+"F8.wireOp",EDGE,"E104");var subQ105=sQuery(id+"F8.wireOp",EDGE,"E102");var subQ106=sQuery(id+"F8.wireOp",EDGE,"E100");var subQ107=sQuery(id+"F8.wireOp",EDGE,"E98");var subQ108=sQuery(id+"F8.wireOp",EDGE,"E96");var subQ109=sQuery(id+"F8.wireOp",EDGE,"E94");var subQ110=sQuery(id+"F8.wireOp",EDGE,"E92");var subQ111=sQuery(id+"F8.wireOp",EDGE,"E90");var subQ112=sQuery(id+"F8.wireOp",EDGE,"E88");var subQ113=sQuery(id+"F8.wireOp",EDGE,"E86");var subQ114=sQuery(id+"F8.wireOp",EDGE,"E84");var subQ115=sQuery(id+"F8.wireOp",EDGE,"E82");var subQ116=sQuery(id+"F8.wireOp",EDGE,"E80");var subQ117=sQuery(id+"F8.wireOp",EDGE,"E78");var subQ118=sQuery(id+"F8.wireOp",EDGE,"E76");var subQ119=sQuery(id+"F8.wireOp",EDGE,"E72.MirrorCS");var subQ120=sQuery(id+"F8.wireOp",EDGE,"E71.MirrorCS");var subQ121=sQuery(id+"F8.wireOp",EDGE,"E70.MirrorCS");var subQ122=sQuery(id+"F8.wireOp",EDGE,"E67.MirrorCS");var subQ123=sQuery(id+"F8.wireOp",EDGE,"E59.MirrorCS");var subQ124=sQuery(id+"F8.wireOp",EDGE,"E58.MirrorCS");var subQ125=sQuery(id+"F8.wireOp",EDGE,"E57");var subQ126=sQuery(id+"F8.wireOp",EDGE,"E56");var subQ127=sQuery(id+"F8.wireOp",EDGE,"E55");var subQ128=sQuery(id+"F8.wireOp",EDGE,"E54");var subQ129=sQuery(id+"F8.wireOp",EDGE,"E50");var subQ130=sQuery(id+"F8.wireOp",EDGE,"E49");var subQ131=sQuery(id+"F8.wireOp",EDGE,"E48.MirrorCS");var subQ132=sQuery(id+"F8.wireOp",EDGE,"E47.MirrorCS");var subQ133=sQuery(id+"F8.wireOp",EDGE,"E34.MirrorCS");var subQ134=sQuery(id+"F8.wireOp",EDGE,"E33");var subQ135=sQuery(id+"F8.wireOp",EDGE,"E32");var subQ136=sQuery(id+"F8.wireOp",EDGE,"E31");var subQ137=sQuery(id+"F8.wireOp",EDGE,"E30");var subQ138=sQuery(id+"F8.wireOp",EDGE,"E29");var subQ139=sQuery(id+"F8.wireOp",EDGE,"E1.0");var subQ140=makeQuery(id+"F15.opExtrude","CAP_FACE",FACE,{"disambiguationData":[OSD([subQ139,subQ83,subQ78,subQ138,subQ137,subQ136,subQ135,subQ134,subQ133,subQ74,subQ70,subQ66,subQ62,subQ58,subQ54,subQ50,subQ46,subQ42,subQ34,subQ29,subQ19,subQ132,subQ131,subQ130,subQ129,subQ57,subQ82,subQ77,subQ128,subQ127,subQ126,subQ125,subQ124,subQ123,subQ73,subQ69,subQ65,subQ53,subQ49,subQ45,subQ41,subQ122,subQ28,subQ18,subQ121,subQ120,subQ119,subQ61,subQ33,subQ118,subQ117,subQ116,subQ115,subQ114,subQ113,subQ112,subQ111,subQ110,subQ109,subQ108,subQ107,subQ106,subQ105,subQ104,subQ103,subQ102,subQ101,subQ100,subQ99,subQ98,subQ97,subQ96,subQ95,subQ94,subQ40,subQ44,subQ48,subQ52,subQ56,subQ81,subQ76,subQ93,subQ92,subQ91,subQ90,subQ89,subQ88,subQ72,subQ68,subQ64,subQ60,subQ87,subQ86,subQ85,subQ17,subQ27,subQ32])],"isStart":true});var subQ141=makeQuery(id+"F16.opExtrude","CAP_FACE",FACE,{"disambiguationData":[OSD([subQ129,subQ122,sQuery(id+"F8.wireOp",EDGE,"E123"),subQ94])],"isStart":true});var subQ142=makeQuery(id+"F16.opExtrude","CAP_FACE",FACE,{"disambiguationData":[OSD([subQ134,subQ124,sQuery(id+"F8.wireOp",EDGE,"E99"),subQ89])],"isStart":true});var subQ143=makeQuery(id+"F16.opExtrude","CAP_FACE",FACE,{"disambiguationData":[OSD([subQ138,subQ128,sQuery(id+"F8.wireOp",EDGE,"E91"),subQ93])],"isStart":true});var subQ144=makeQuery(id+"F16.opExtrude","CAP_FACE",FACE,{"disambiguationData":[OSD([subQ137,subQ127,sQuery(id+"F8.wireOp",EDGE,"E93"),subQ92])],"isStart":true});var subQ145=makeQuery(id+"F19.opExtrude","CAP_FACE",FACE,{"disambiguationData":[OSD([subQ25,subQ24,subQ15,subQ23,subQ22,subQ21])],"isStart":true});var subQ146=makeQuery(id+"F16.opExtrude","CAP_FACE",FACE,{"disambiguationData":[OSD([subQ136,subQ126,sQuery(id+"F8.wireOp",EDGE,"E95"),subQ91])],"isStart":true});var subQ147=makeQuery(id+"F15.opExtrude","CAP_FACE",FACE,{"disambiguationData":[OSD([subQ139,subQ83,subQ78,subQ138,subQ137,subQ136,subQ135,subQ134,subQ133,subQ74,subQ70,subQ66,subQ62,subQ58,subQ54,subQ50,subQ46,subQ42,subQ34,subQ29,subQ19,subQ132,subQ131,subQ130,subQ129,subQ57,subQ82,subQ77,subQ128,subQ127,subQ126,subQ125,subQ124,subQ123,subQ73,subQ69,subQ65,subQ53,subQ49,subQ45,subQ41,subQ122,subQ28,subQ18,subQ121,subQ120,subQ119,subQ61,subQ33,subQ118,subQ117,subQ116,subQ115,subQ114,subQ113,subQ112,subQ111,subQ110,subQ109,subQ108,subQ107,subQ106,subQ105,subQ104,subQ103,subQ102,subQ101,subQ100,subQ99,subQ98,subQ97,subQ96,subQ95,subQ94,subQ40,subQ44,subQ48,subQ52,subQ56,subQ81,subQ76,subQ93,subQ92,subQ91,subQ90,subQ89,subQ88,subQ72,subQ68,subQ64,subQ60,subQ87,subQ86,subQ85,subQ17,subQ27,subQ32])],"isStart":false});var subQ148=makeQuery(id+"F16.opExtrude","CAP_FACE",FACE,{"disambiguationData":[OSD([subQ135,subQ125,sQuery(id+"F8.wireOp",EDGE,"E97"),subQ90])],"isStart":true});var subQ149=makeQuery(id+"F19.opExtrude","SWEPT_FACE",FACE,{"disambiguationData":[OSD([subQ21])]});var subQ150=makeQuery(id+"F16.opExtrude","CAP_FACE",FACE,{"disambiguationData":[OSD([subQ133,subQ123,sQuery(id+"F8.wireOp",EDGE,"E101"),subQ88])],"isStart":true});var subQ151=makeQuery(id+"F16.opExtrude","CAP_FACE",FACE,{"disambiguationData":[OSD([subQ132,subQ121,sQuery(id+"F8.wireOp",EDGE,"E115"),subQ85])],"isStart":true});var subQ152=makeQuery(id+"F16.opExtrude","CAP_FACE",FACE,{"disambiguationData":[OSD([subQ131,subQ120,sQuery(id+"F8.wireOp",EDGE,"E113"),subQ86])],"isStart":true});var subQ153=makeQuery(id+"F16.opExtrude","CAP_FACE",FACE,{"disambiguationData":[OSD([subQ130,subQ119,sQuery(id+"F8.wireOp",EDGE,"E111"),subQ87])],"isStart":true});var subQ154=makeQuery(id+"F18.opRevolve","SWEPT_FACE",FACE,{"disambiguationData":[OSD([subQ36])]});var subQ155=makeQuery(id+"F19.opExtrude","SWEPT_FACE",FACE,{"disambiguationData":[OSD([subQ24])]});var subQ156=makeQuery(id+"F19.opExtrude","SWEPT_FACE",FACE,{"disambiguationData":[OSD([subQ22])]});Q7=makeQuery(id+"F38.opFillet","BLEND_EDGE",EDGE,{"blendedFrom":[makeQuery(id+"F21.boolean.opBoolean","INTERSECT",EDGE,{"derivedFrom":[makeQuery(id+"F20.boolean.opBoolean","SPLIT",FACE,{"disambiguationData":[TD([subQ31])],"derivedFrom":makeQuery(id+"F19.boolean.opBoolean","SPLIT",FACE,{"disambiguationData":[TD([makeQuery(id+"F15.opExtrude","SWEPT_FACE",FACE,{"disambiguationData":[OSD([subQ139])]}),subQ140,subQ147,subQ84,subQ79,subQ143,subQ144,subQ146,subQ148,subQ142,subQ150,subQ75,subQ71,subQ67,subQ63,subQ59,subQ55,subQ51,subQ47,subQ43,subQ35,subQ30,subQ20,subQ151,subQ152,subQ153,subQ141,subQ80,subQ39,subQ31,subQ154,subQ145,subQ26,subQ155,subQ16,subQ156,subQ149])],"derivedFrom":makeQuery(id+"F18.boolean.opBoolean","MERGE",FACE,{"derivedFrom":[subQ10,subQ9]})})}),subQ12]}),makeQuery(id+"F24.boolean.opBoolean","SPLIT",FACE,{"disambiguationData":[TD([subQ11])],"derivedFrom":makeQuery(id+"F23.boolean.opBoolean","MERGE",FACE,{"derivedFrom":[subQ16,subQ14,makeQuery(id+"F23.opExtrude","CAP_FACE",FACE,{"disambiguationData":[OSD([sQuery(id+"F13.wireOp",EDGE,"E297.MirrorCS"),sQuery(id+"F13.wireOp",EDGE,"E307"),sQuery(id+"F13.wireOp",EDGE,"E308"),subQ13,sQuery(id+"F13.wireOp",EDGE,"E310.0"),sQuery(id+"F13.wireOp",EDGE,"E310.1"),sQuery(id+"F13.wireOp",EDGE,"E310.2")])],"isStart":false})]})})],"blendedInto":[makeQuery(id+"F24.boolean.opBoolean","SPLIT",FACE,{"disambiguationData":[TD([subQ11])],"derivedFrom":makeQuery(id+"F23.boolean.opBoolean","MERGE",FACE,{"derivedFrom":[subQ16,subQ14,makeQuery(id+"F23.opExtrude","CAP_FACE",FACE,{"disambiguationData":[OSD([sQuery(id+"F13.wireOp",EDGE,"E297.MirrorCS"),sQuery(id+"F13.wireOp",EDGE,"E307"),sQuery(id+"F13.wireOp",EDGE,"E308"),subQ13,sQuery(id+"F13.wireOp",EDGE,"E310.0"),sQuery(id+"F13.wireOp",EDGE,"E310.1"),sQuery(id+"F13.wireOp",EDGE,"E310.2")])],"isStart":false})]})})]});}
            var Q8;
            {var subQ0=sQuery(id+"F12.wireOp",EDGE,"E290");var subQ1=sQuery(id+"F12.wireOp",EDGE,"E289");var subQ2=sQuery(id+"F12.wireOp",EDGE,"E288");var subQ3=sQuery(id+"F12.wireOp",EDGE,"E287");var subQ4=sQuery(id+"F12.wireOp",EDGE,"E286");var subQ5=sQuery(id+"F12.wireOp",EDGE,"E285");var subQ6=makeQuery(id+"F19.opExtrude","CAP_FACE",FACE,{"disambiguationData":[OSD([subQ5,subQ4,subQ3,subQ2,subQ1,subQ0])],"isStart":false});var subQ7=sQuery(id+"F9.wireOp",EDGE,"E150");var subQ8=makeQuery(id+"F18.opRevolve","SWEPT_FACE",FACE,{"disambiguationData":[OSD([subQ7])]});var subQ9=makeQuery(id+"F19.opExtrude","SWEPT_FACE",FACE,{"disambiguationData":[OSD([subQ4])]});var subQ10=sQuery(id+"F13.wireOp",EDGE,"E307");var subQ11=makeQuery(id+"F19.opExtrude","CAP_FACE",FACE,{"disambiguationData":[OSD([subQ5,subQ4,subQ3,subQ2,subQ1,subQ0])],"isStart":true});var subQ12=makeQuery(id+"F17.opRevolve","SWEPT_FACE",FACE,{"disambiguationData":[OSD([subQ7])]});var subQ13=makeQuery(id+"F21.opExtrude","SWEPT_FACE",FACE,{"disambiguationData":[OSD([sQuery(id+"F13.wireOp",EDGE,"E295.MirrorCS")])]});var subQ14=sQuery(id+"F11.wireOp",EDGE,"E261");var subQ15=makeQuery(id+"F20.opExtrude","SWEPT_FACE",FACE,{"disambiguationData":[OSD([subQ14])]});var subQ16=makeQuery(id+"F19.opExtrude","SWEPT_FACE",FACE,{"disambiguationData":[OSD([subQ3])]});var subQ17=sQuery(id+"F8.wireOp",EDGE,"E145");var subQ18=sQuery(id+"F8.wireOp",EDGE,"E69.MirrorCS");var subQ19=sQuery(id+"F8.wireOp",EDGE,"E46.MirrorCS");var subQ20=makeQuery(id+"F16.opExtrude","CAP_FACE",FACE,{"disambiguationData":[OSD([subQ19,subQ18,sQuery(id+"F8.wireOp",EDGE,"E117"),subQ17])],"isStart":true});var subQ21=sQuery(id+"F8.wireOp",EDGE,"E146");var subQ22=sQuery(id+"F8.wireOp",EDGE,"E68.MirrorCS");var subQ23=sQuery(id+"F8.wireOp",EDGE,"E45.MirrorCS");var subQ24=makeQuery(id+"F16.opExtrude","CAP_FACE",FACE,{"disambiguationData":[OSD([subQ23,subQ22,sQuery(id+"F8.wireOp",EDGE,"E120"),subQ21])],"isStart":true});var subQ25=makeQuery(id+"F18.opRevolve","SWEPT_FACE",FACE,{"disambiguationData":[OSD([sQuery(id+"F9.wireOp",EDGE,"E157")])]});var subQ26=sQuery(id+"F8.wireOp",EDGE,"E147");var subQ27=sQuery(id+"F8.wireOp",EDGE,"E74");var subQ28=sQuery(id+"F8.wireOp",EDGE,"E44.MirrorCS");var subQ29=makeQuery(id+"F16.opExtrude","CAP_FACE",FACE,{"disambiguationData":[OSD([subQ28,subQ27,sQuery(id+"F8.wireOp",EDGE,"E121"),subQ26])],"isStart":true});var subQ30=sQuery(id+"F9.wireOp",EDGE,"E164");var subQ31=sQuery(id+"F9.wireOp",EDGE,"E152");var subQ32=sQuery(id+"F9.wireOp",EDGE,"E151");var subQ33=makeQuery(id+"F17.opRevolve","CAP_FACE",FACE,{"disambiguationData":[OSD([subQ7,subQ32,subQ31,subQ30])],"isStart":false});var subQ34=sQuery(id+"F8.wireOp",EDGE,"E125");var subQ35=sQuery(id+"F8.wireOp",EDGE,"E66.MirrorCS");var subQ36=sQuery(id+"F8.wireOp",EDGE,"E43.MirrorCS");var subQ37=makeQuery(id+"F16.opExtrude","CAP_FACE",FACE,{"disambiguationData":[OSD([subQ36,subQ35,sQuery(id+"F8.wireOp",EDGE,"E77"),subQ34])],"isStart":true});var subQ38=sQuery(id+"F8.wireOp",EDGE,"E126");var subQ39=sQuery(id+"F8.wireOp",EDGE,"E65.MirrorCS");var subQ40=sQuery(id+"F8.wireOp",EDGE,"E42.MirrorCS");var subQ41=makeQuery(id+"F16.opExtrude","CAP_FACE",FACE,{"disambiguationData":[OSD([subQ40,subQ39,sQuery(id+"F8.wireOp",EDGE,"E79"),subQ38])],"isStart":true});var subQ42=sQuery(id+"F8.wireOp",EDGE,"E127");var subQ43=sQuery(id+"F8.wireOp",EDGE,"E64.MirrorCS");var subQ44=sQuery(id+"F8.wireOp",EDGE,"E41.MirrorCS");var subQ45=makeQuery(id+"F16.opExtrude","CAP_FACE",FACE,{"disambiguationData":[OSD([subQ44,subQ43,sQuery(id+"F8.wireOp",EDGE,"E81"),subQ42])],"isStart":true});var subQ46=sQuery(id+"F8.wireOp",EDGE,"E128");var subQ47=sQuery(id+"F8.wireOp",EDGE,"E63.MirrorCS");var subQ48=sQuery(id+"F8.wireOp",EDGE,"E40.MirrorCS");var subQ49=makeQuery(id+"F16.opExtrude","CAP_FACE",FACE,{"disambiguationData":[OSD([subQ48,subQ47,sQuery(id+"F8.wireOp",EDGE,"E83"),subQ46])],"isStart":true});var subQ50=sQuery(id+"F8.wireOp",EDGE,"E129");var subQ51=sQuery(id+"F8.wireOp",EDGE,"E51");var subQ52=sQuery(id+"F8.wireOp",EDGE,"E39.MirrorCS");var subQ53=makeQuery(id+"F16.opExtrude","CAP_FACE",FACE,{"disambiguationData":[OSD([subQ52,subQ51,sQuery(id+"F8.wireOp",EDGE,"E85"),subQ50])],"isStart":true});var subQ54=sQuery(id+"F8.wireOp",EDGE,"E141");var subQ55=sQuery(id+"F8.wireOp",EDGE,"E73");var subQ56=sQuery(id+"F8.wireOp",EDGE,"E38.MirrorCS");var subQ57=makeQuery(id+"F16.opExtrude","CAP_FACE",FACE,{"disambiguationData":[OSD([subQ56,subQ55,sQuery(id+"F8.wireOp",EDGE,"E109"),subQ54])],"isStart":true});var subQ58=sQuery(id+"F8.wireOp",EDGE,"E140");var subQ59=sQuery(id+"F8.wireOp",EDGE,"E62.MirrorCS");var subQ60=sQuery(id+"F8.wireOp",EDGE,"E37.MirrorCS");var subQ61=makeQuery(id+"F16.opExtrude","CAP_FACE",FACE,{"disambiguationData":[OSD([subQ60,subQ59,sQuery(id+"F8.wireOp",EDGE,"E107"),subQ58])],"isStart":true});var subQ62=sQuery(id+"F8.wireOp",EDGE,"E139");var subQ63=sQuery(id+"F8.wireOp",EDGE,"E61.MirrorCS");var subQ64=sQuery(id+"F8.wireOp",EDGE,"E36.MirrorCS");var subQ65=makeQuery(id+"F16.opExtrude","CAP_FACE",FACE,{"disambiguationData":[OSD([subQ64,subQ63,sQuery(id+"F8.wireOp",EDGE,"E105"),subQ62])],"isStart":true});var subQ66=sQuery(id+"F8.wireOp",EDGE,"E138");var subQ67=sQuery(id+"F8.wireOp",EDGE,"E60.MirrorCS");var subQ68=sQuery(id+"F8.wireOp",EDGE,"E35.MirrorCS");var subQ69=makeQuery(id+"F16.opExtrude","CAP_FACE",FACE,{"disambiguationData":[OSD([subQ68,subQ67,sQuery(id+"F8.wireOp",EDGE,"E103"),subQ66])],"isStart":true});var subQ70=sQuery(id+"F8.wireOp",EDGE,"E131");var subQ71=sQuery(id+"F8.wireOp",EDGE,"E53");var subQ72=sQuery(id+"F8.wireOp",EDGE,"E28");var subQ73=makeQuery(id+"F16.opExtrude","CAP_FACE",FACE,{"disambiguationData":[OSD([subQ72,subQ71,sQuery(id+"F8.wireOp",EDGE,"E89"),subQ70])],"isStart":true});var subQ74=makeQuery(id+"F17.opRevolve","CAP_FACE",FACE,{"disambiguationData":[OSD([subQ7,subQ32,subQ31,subQ30])],"isStart":true});var subQ75=sQuery(id+"F8.wireOp",EDGE,"E130");var subQ76=sQuery(id+"F8.wireOp",EDGE,"E52");var subQ77=sQuery(id+"F8.wireOp",EDGE,"E27");var subQ78=makeQuery(id+"F16.opExtrude","CAP_FACE",FACE,{"disambiguationData":[OSD([subQ77,subQ76,sQuery(id+"F8.wireOp",EDGE,"E87"),subQ75])],"isStart":true});var subQ79=sQuery(id+"F8.wireOp",EDGE,"E144");var subQ80=sQuery(id+"F8.wireOp",EDGE,"E143");var subQ81=sQuery(id+"F8.wireOp",EDGE,"E142");var subQ82=sQuery(id+"F8.wireOp",EDGE,"E137");var subQ83=sQuery(id+"F8.wireOp",EDGE,"E136");var subQ84=sQuery(id+"F8.wireOp",EDGE,"E135");var subQ85=sQuery(id+"F8.wireOp",EDGE,"E134");var subQ86=sQuery(id+"F8.wireOp",EDGE,"E133");var subQ87=sQuery(id+"F8.wireOp",EDGE,"E132");var subQ88=sQuery(id+"F8.wireOp",EDGE,"E124");var subQ89=sQuery(id+"F8.wireOp",EDGE,"E122");var subQ90=sQuery(id+"F8.wireOp",EDGE,"E119");var subQ91=sQuery(id+"F8.wireOp",EDGE,"E118");var subQ92=sQuery(id+"F8.wireOp",EDGE,"E116");var subQ93=sQuery(id+"F8.wireOp",EDGE,"E114");var subQ94=sQuery(id+"F8.wireOp",EDGE,"E112");var subQ95=sQuery(id+"F8.wireOp",EDGE,"E110");var subQ96=sQuery(id+"F8.wireOp",EDGE,"E108");var subQ97=sQuery(id+"F8.wireOp",EDGE,"E106");var subQ98=sQuery(id+"F8.wireOp",EDGE,"E104");var subQ99=sQuery(id+"F8.wireOp",EDGE,"E102");var subQ100=sQuery(id+"F8.wireOp",EDGE,"E100");var subQ101=sQuery(id+"F8.wireOp",EDGE,"E98");var subQ102=sQuery(id+"F8.wireOp",EDGE,"E96");var subQ103=sQuery(id+"F8.wireOp",EDGE,"E94");var subQ104=sQuery(id+"F8.wireOp",EDGE,"E92");var subQ105=sQuery(id+"F8.wireOp",EDGE,"E90");var subQ106=sQuery(id+"F8.wireOp",EDGE,"E88");var subQ107=sQuery(id+"F8.wireOp",EDGE,"E86");var subQ108=sQuery(id+"F8.wireOp",EDGE,"E84");var subQ109=sQuery(id+"F8.wireOp",EDGE,"E82");var subQ110=sQuery(id+"F8.wireOp",EDGE,"E80");var subQ111=sQuery(id+"F8.wireOp",EDGE,"E78");var subQ112=sQuery(id+"F8.wireOp",EDGE,"E76");var subQ113=sQuery(id+"F8.wireOp",EDGE,"E72.MirrorCS");var subQ114=sQuery(id+"F8.wireOp",EDGE,"E71.MirrorCS");var subQ115=sQuery(id+"F8.wireOp",EDGE,"E70.MirrorCS");var subQ116=sQuery(id+"F8.wireOp",EDGE,"E67.MirrorCS");var subQ117=sQuery(id+"F8.wireOp",EDGE,"E59.MirrorCS");var subQ118=sQuery(id+"F8.wireOp",EDGE,"E58.MirrorCS");var subQ119=sQuery(id+"F8.wireOp",EDGE,"E57");var subQ120=sQuery(id+"F8.wireOp",EDGE,"E56");var subQ121=sQuery(id+"F8.wireOp",EDGE,"E55");var subQ122=sQuery(id+"F8.wireOp",EDGE,"E54");var subQ123=sQuery(id+"F8.wireOp",EDGE,"E50");var subQ124=sQuery(id+"F8.wireOp",EDGE,"E49");var subQ125=sQuery(id+"F8.wireOp",EDGE,"E48.MirrorCS");var subQ126=sQuery(id+"F8.wireOp",EDGE,"E47.MirrorCS");var subQ127=sQuery(id+"F8.wireOp",EDGE,"E34.MirrorCS");var subQ128=sQuery(id+"F8.wireOp",EDGE,"E33");var subQ129=sQuery(id+"F8.wireOp",EDGE,"E32");var subQ130=sQuery(id+"F8.wireOp",EDGE,"E31");var subQ131=sQuery(id+"F8.wireOp",EDGE,"E30");var subQ132=sQuery(id+"F8.wireOp",EDGE,"E29");var subQ133=sQuery(id+"F8.wireOp",EDGE,"E1.0");var subQ134=makeQuery(id+"F15.opExtrude","CAP_FACE",FACE,{"disambiguationData":[OSD([subQ133,subQ77,subQ72,subQ132,subQ131,subQ130,subQ129,subQ128,subQ127,subQ68,subQ64,subQ60,subQ56,subQ52,subQ48,subQ44,subQ40,subQ36,subQ28,subQ23,subQ19,subQ126,subQ125,subQ124,subQ123,subQ51,subQ76,subQ71,subQ122,subQ121,subQ120,subQ119,subQ118,subQ117,subQ67,subQ63,subQ59,subQ47,subQ43,subQ39,subQ35,subQ116,subQ22,subQ18,subQ115,subQ114,subQ113,subQ55,subQ27,subQ112,subQ111,subQ110,subQ109,subQ108,subQ107,subQ106,subQ105,subQ104,subQ103,subQ102,subQ101,subQ100,subQ99,subQ98,subQ97,subQ96,subQ95,subQ94,subQ93,subQ92,subQ91,subQ90,subQ89,subQ88,subQ34,subQ38,subQ42,subQ46,subQ50,subQ75,subQ70,subQ87,subQ86,subQ85,subQ84,subQ83,subQ82,subQ66,subQ62,subQ58,subQ54,subQ81,subQ80,subQ79,subQ17,subQ21,subQ26])],"isStart":true});var subQ135=makeQuery(id+"F16.opExtrude","CAP_FACE",FACE,{"disambiguationData":[OSD([subQ123,subQ116,sQuery(id+"F8.wireOp",EDGE,"E123"),subQ88])],"isStart":true});var subQ136=makeQuery(id+"F16.opExtrude","CAP_FACE",FACE,{"disambiguationData":[OSD([subQ128,subQ118,sQuery(id+"F8.wireOp",EDGE,"E99"),subQ83])],"isStart":true});var subQ138=makeQuery(id+"F16.opExtrude","CAP_FACE",FACE,{"disambiguationData":[OSD([subQ132,subQ122,sQuery(id+"F8.wireOp",EDGE,"E91"),subQ87])],"isStart":true});var subQ139=makeQuery(id+"F16.opExtrude","CAP_FACE",FACE,{"disambiguationData":[OSD([subQ131,subQ121,sQuery(id+"F8.wireOp",EDGE,"E93"),subQ86])],"isStart":true});var subQ140=makeQuery(id+"F16.opExtrude","CAP_FACE",FACE,{"disambiguationData":[OSD([subQ130,subQ120,sQuery(id+"F8.wireOp",EDGE,"E95"),subQ85])],"isStart":true});var subQ145=makeQuery(id+"F15.opExtrude","CAP_FACE",FACE,{"disambiguationData":[OSD([subQ133,subQ77,subQ72,subQ132,subQ131,subQ130,subQ129,subQ128,subQ127,subQ68,subQ64,subQ60,subQ56,subQ52,subQ48,subQ44,subQ40,subQ36,subQ28,subQ23,subQ19,subQ126,subQ125,subQ124,subQ123,subQ51,subQ76,subQ71,subQ122,subQ121,subQ120,subQ119,subQ118,subQ117,subQ67,subQ63,subQ59,subQ47,subQ43,subQ39,subQ35,subQ116,subQ22,subQ18,subQ115,subQ114,subQ113,subQ55,subQ27,subQ112,subQ111,subQ110,subQ109,subQ108,subQ107,subQ106,subQ105,subQ104,subQ103,subQ102,subQ101,subQ100,subQ99,subQ98,subQ97,subQ96,subQ95,subQ94,subQ93,subQ92,subQ91,subQ90,subQ89,subQ88,subQ34,subQ38,subQ42,subQ46,subQ50,subQ75,subQ70,subQ87,subQ86,subQ85,subQ84,subQ83,subQ82,subQ66,subQ62,subQ58,subQ54,subQ81,subQ80,subQ79,subQ17,subQ21,subQ26])],"isStart":false});var subQ146=makeQuery(id+"F16.opExtrude","CAP_FACE",FACE,{"disambiguationData":[OSD([subQ129,subQ119,sQuery(id+"F8.wireOp",EDGE,"E97"),subQ84])],"isStart":true});var subQ147=makeQuery(id+"F19.opExtrude","SWEPT_FACE",FACE,{"disambiguationData":[OSD([subQ0])]});var subQ148=makeQuery(id+"F16.opExtrude","CAP_FACE",FACE,{"disambiguationData":[OSD([subQ127,subQ117,sQuery(id+"F8.wireOp",EDGE,"E101"),subQ82])],"isStart":true});var subQ149=makeQuery(id+"F16.opExtrude","CAP_FACE",FACE,{"disambiguationData":[OSD([subQ126,subQ115,sQuery(id+"F8.wireOp",EDGE,"E115"),subQ79])],"isStart":true});var subQ150=makeQuery(id+"F16.opExtrude","CAP_FACE",FACE,{"disambiguationData":[OSD([subQ125,subQ114,sQuery(id+"F8.wireOp",EDGE,"E113"),subQ80])],"isStart":true});var subQ151=makeQuery(id+"F16.opExtrude","CAP_FACE",FACE,{"disambiguationData":[OSD([subQ124,subQ113,sQuery(id+"F8.wireOp",EDGE,"E111"),subQ81])],"isStart":true});var subQ152=makeQuery(id+"F18.opRevolve","SWEPT_FACE",FACE,{"disambiguationData":[OSD([subQ30])]});var subQ153=makeQuery(id+"F19.opExtrude","SWEPT_FACE",FACE,{"disambiguationData":[OSD([subQ1])]});Q8=makeQuery(id+"F38.opFillet","BLEND_EDGE",EDGE,{"blendedFrom":[makeQuery(id+"F21.boolean.opBoolean","INTERSECT",EDGE,{"derivedFrom":[makeQuery(id+"F20.boolean.opBoolean","SPLIT",FACE,{"disambiguationData":[TD([subQ25])],"derivedFrom":makeQuery(id+"F19.boolean.opBoolean","SPLIT",FACE,{"disambiguationData":[TD([makeQuery(id+"F15.opExtrude","SWEPT_FACE",FACE,{"disambiguationData":[OSD([subQ133])]}),subQ134,subQ145,subQ78,subQ73,subQ138,subQ139,subQ140,subQ146,subQ136,subQ148,subQ69,subQ65,subQ61,subQ57,subQ53,subQ49,subQ45,subQ41,subQ37,subQ29,subQ24,subQ20,subQ149,subQ150,subQ151,subQ135,subQ74,subQ33,subQ25,subQ152,subQ11,subQ6,subQ9,subQ16,subQ153,subQ147])],"derivedFrom":makeQuery(id+"F18.boolean.opBoolean","MERGE",FACE,{"derivedFrom":[subQ12,subQ8]})})}),subQ13]}),makeQuery(id+"F24.boolean.opBoolean","SPLIT",FACE,{"disambiguationData":[TD([subQ9])],"derivedFrom":makeQuery(id+"F23.boolean.opBoolean","MERGE",FACE,{"derivedFrom":[subQ16,subQ15,makeQuery(id+"F23.opExtrude","CAP_FACE",FACE,{"disambiguationData":[OSD([sQuery(id+"F13.wireOp",EDGE,"E297.MirrorCS"),subQ10,sQuery(id+"F13.wireOp",EDGE,"E308"),sQuery(id+"F13.wireOp",EDGE,"E309"),sQuery(id+"F13.wireOp",EDGE,"E310.0"),sQuery(id+"F13.wireOp",EDGE,"E310.1"),sQuery(id+"F13.wireOp",EDGE,"E310.2")])],"isStart":false})]})})],"blendedInto":[makeQuery(id+"F24.boolean.opBoolean","SPLIT",FACE,{"disambiguationData":[TD([subQ9])],"derivedFrom":makeQuery(id+"F23.boolean.opBoolean","MERGE",FACE,{"derivedFrom":[subQ16,subQ15,makeQuery(id+"F23.opExtrude","CAP_FACE",FACE,{"disambiguationData":[OSD([sQuery(id+"F13.wireOp",EDGE,"E297.MirrorCS"),subQ10,sQuery(id+"F13.wireOp",EDGE,"E308"),sQuery(id+"F13.wireOp",EDGE,"E309"),sQuery(id+"F13.wireOp",EDGE,"E310.0"),sQuery(id+"F13.wireOp",EDGE,"E310.1"),sQuery(id+"F13.wireOp",EDGE,"E310.2")])],"isStart":false})]})})]});}
            var Q9;
            Q9=makeQuery(id+"F25.opExtrude","CAP_EDGE",EDGE,{"disambiguationData":[OSD([sQuery(id+"F10.wireOp",EDGE,"E233")])],"isStart":true});
            var Q10;
            Q10=makeQuery(id+"F25.opExtrude","CAP_EDGE",EDGE,{"disambiguationData":[OSD([sQuery(id+"F10.wireOp",EDGE,"E234")])],"isStart":true});
            var Q11;
            Q11=makeQuery(id+"F25.opExtrude","CAP_EDGE",EDGE,{"disambiguationData":[OSD([sQuery(id+"F10.wireOp",EDGE,"oL6OTD61-6akg-XuXO-bSg7-LTXE6IEmyDXN")])],"isStart":true});
            var Q12;
            Q12=makeQuery(id+"F37.opExtrude","SWEPT_EDGE",EDGE,{"disambiguationData":[OSD([sQuery(id+"F31.wireOp",EDGE,"E362.0"),sQuery(id+"F31.wireOp",EDGE,"E364")])]});
            var Q13;
            Q13=makeQuery(id+"F37.opExtrude","SWEPT_EDGE",EDGE,{"disambiguationData":[OSD([sQuery(id+"F31.wireOp",EDGE,"E362.0"),sQuery(id+"F31.wireOp",EDGE,"E363")])]});
            var Q14;
            Q14=makeQuery(id+"F37.opExtrude","SWEPT_EDGE",EDGE,{"disambiguationData":[OSD([sQuery(id+"F31.wireOp",EDGE,"E360"),sQuery(id+"F31.wireOp",EDGE,"E364")])]});
            var Q15;
            Q15=makeQuery(id+"F37.opExtrude","SWEPT_EDGE",EDGE,{"disambiguationData":[OSD([sQuery(id+"F31.wireOp",EDGE,"E360"),sQuery(id+"F31.wireOp",EDGE,"E363")])]});
            fillet(context, id + "F39", {"entities" : qUnion([Q0, Q1, Q2, Q3, Q4, Q5, Q6, Q7, Q8, Q9, Q10, Q11, Q12, Q13, Q14, Q15]), "radius" : 2.6 * mm, "tangentPropagation" : true, "allowEdgeOverflow" : false});
        }
        {
            var Q0;
            Q0=makeQuery(id+"F16.opExtrude","CAP_EDGE",EDGE,{"disambiguationData":[OSD([sQuery(id+"F8.wireOp",EDGE,"E77")])],"isStart":false});
            var Q1;
            Q1=makeQuery(id+"F16.opExtrude","CAP_EDGE",EDGE,{"disambiguationData":[OSD([sQuery(id+"F8.wireOp",EDGE,"E79")])],"isStart":false});
            var Q2;
            Q2=makeQuery(id+"F16.opExtrude","CAP_EDGE",EDGE,{"disambiguationData":[OSD([sQuery(id+"F8.wireOp",EDGE,"E81")])],"isStart":false});
            var Q3;
            Q3=makeQuery(id+"F16.opExtrude","CAP_EDGE",EDGE,{"disambiguationData":[OSD([sQuery(id+"F8.wireOp",EDGE,"E83")])],"isStart":false});
            var Q4;
            Q4=makeQuery(id+"F16.opExtrude","CAP_EDGE",EDGE,{"disambiguationData":[OSD([sQuery(id+"F8.wireOp",EDGE,"E85")])],"isStart":false});
            var Q5;
            Q5=makeQuery(id+"F16.opExtrude","CAP_EDGE",EDGE,{"disambiguationData":[OSD([sQuery(id+"F8.wireOp",EDGE,"E87")])],"isStart":false});
            var Q6;
            Q6=makeQuery(id+"F16.opExtrude","CAP_EDGE",EDGE,{"disambiguationData":[OSD([sQuery(id+"F8.wireOp",EDGE,"E89")])],"isStart":false});
            var Q7;
            Q7=makeQuery(id+"F16.opExtrude","CAP_EDGE",EDGE,{"disambiguationData":[OSD([sQuery(id+"F8.wireOp",EDGE,"E91")])],"isStart":false});
            var Q8;
            Q8=makeQuery(id+"F16.opExtrude","CAP_EDGE",EDGE,{"disambiguationData":[OSD([sQuery(id+"F8.wireOp",EDGE,"E93")])],"isStart":false});
            var Q9;
            Q9=makeQuery(id+"F16.opExtrude","CAP_EDGE",EDGE,{"disambiguationData":[OSD([sQuery(id+"F8.wireOp",EDGE,"E95")])],"isStart":false});
            var Q10;
            Q10=makeQuery(id+"F16.opExtrude","CAP_EDGE",EDGE,{"disambiguationData":[OSD([sQuery(id+"F8.wireOp",EDGE,"E123")])],"isStart":false});
            var Q11;
            Q11=makeQuery(id+"F16.opExtrude","CAP_EDGE",EDGE,{"disambiguationData":[OSD([sQuery(id+"F8.wireOp",EDGE,"E121")])],"isStart":false});
            var Q12;
            Q12=makeQuery(id+"F16.opExtrude","CAP_EDGE",EDGE,{"disambiguationData":[OSD([sQuery(id+"F8.wireOp",EDGE,"E120")])],"isStart":false});
            var Q13;
            Q13=makeQuery(id+"F16.opExtrude","CAP_EDGE",EDGE,{"disambiguationData":[OSD([sQuery(id+"F8.wireOp",EDGE,"E117")])],"isStart":false});
            var Q14;
            Q14=makeQuery(id+"F16.opExtrude","CAP_EDGE",EDGE,{"disambiguationData":[OSD([sQuery(id+"F8.wireOp",EDGE,"E115")])],"isStart":false});
            var Q15;
            Q15=makeQuery(id+"F16.opExtrude","CAP_EDGE",EDGE,{"disambiguationData":[OSD([sQuery(id+"F8.wireOp",EDGE,"E113")])],"isStart":false});
            var Q16;
            Q16=makeQuery(id+"F16.opExtrude","CAP_EDGE",EDGE,{"disambiguationData":[OSD([sQuery(id+"F8.wireOp",EDGE,"E111")])],"isStart":false});
            var Q17;
            Q17=makeQuery(id+"F16.opExtrude","CAP_EDGE",EDGE,{"disambiguationData":[OSD([sQuery(id+"F8.wireOp",EDGE,"E109")])],"isStart":false});
            var Q18;
            Q18=makeQuery(id+"F16.opExtrude","CAP_EDGE",EDGE,{"disambiguationData":[OSD([sQuery(id+"F8.wireOp",EDGE,"E107")])],"isStart":false});
            var Q19;
            Q19=makeQuery(id+"F16.opExtrude","CAP_EDGE",EDGE,{"disambiguationData":[OSD([sQuery(id+"F8.wireOp",EDGE,"E105")])],"isStart":false});
            var Q20;
            Q20=makeQuery(id+"F16.opExtrude","CAP_EDGE",EDGE,{"disambiguationData":[OSD([sQuery(id+"F8.wireOp",EDGE,"E103")])],"isStart":false});
            var Q21;
            Q21=makeQuery(id+"F16.opExtrude","CAP_EDGE",EDGE,{"disambiguationData":[OSD([sQuery(id+"F8.wireOp",EDGE,"E101")])],"isStart":false});
            var Q22;
            Q22=makeQuery(id+"F16.opExtrude","CAP_EDGE",EDGE,{"disambiguationData":[OSD([sQuery(id+"F8.wireOp",EDGE,"E99")])],"isStart":false});
            var Q23;
            Q23=makeQuery(id+"F16.opExtrude","CAP_EDGE",EDGE,{"disambiguationData":[OSD([sQuery(id+"F8.wireOp",EDGE,"E97")])],"isStart":false});
            fillet(context, id + "F40", {"entities" : qUnion([Q0, Q1, Q2, Q3, Q4, Q5, Q6, Q7, Q8, Q9, Q10, Q11, Q12, Q13, Q14, Q15, Q16, Q17, Q18, Q19, Q20, Q21, Q22, Q23]), "radius" : 3 * mm, "tangentPropagation" : true, "allowEdgeOverflow" : false});
        }
    });
